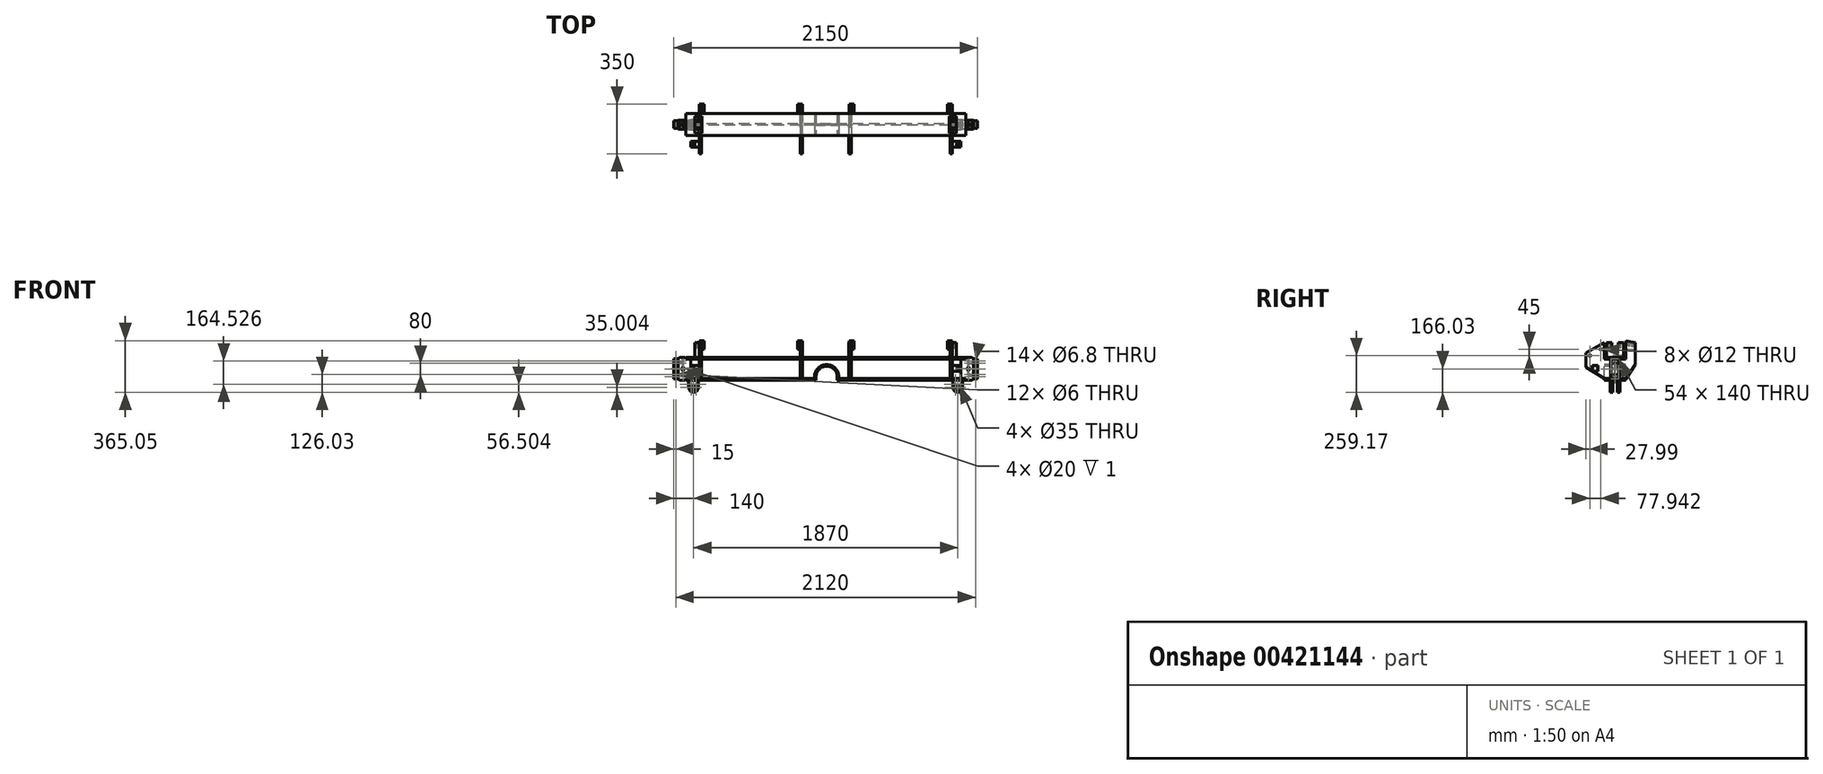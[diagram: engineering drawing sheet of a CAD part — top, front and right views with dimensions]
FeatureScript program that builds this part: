
annotation { "Feature Type Name" : "Feature", "Feature Type Description" : "" }
export const myFeature = defineFeature(function(context is Context, id is Id, definition is map)
    precondition{}
    {
        {
            var Q0;
            Q0=qCreatedBy(makeId("Right.planeOp"),FACE);
            var sketch = newSketch(context, id + "F0", { "sketchPlane" : qUnion([Q0])});
            skLineSegment(sketch, "E0.bottom", {"start": v(-77.22, 81.03) * mm, "end": v(77.22, 81.03) * mm});
            skLineSegment(sketch, "E0.top", {"start": v(-77.22, -81.03) * mm, "end": v(77.22, -81.03) * mm});
            skLineSegment(sketch, "E0.left", {"start": v(-77.22, 81.03) * mm, "end": v(-77.22, 69.47) * mm});
            skLineSegment(sketch, "E0.right", {"start": v(77.22, 81.03) * mm, "end": v(77.22, 69.47) * mm});
            skPoint(sketch, "E0.middle", {"position": v(0, 0) * mm});
            skLineSegment(sketch, "E1", {"start": v(0, 87.3) * mm, "end": v(0, -92.44) * mm, "construction": true});
            skLineSegment(sketch, "E2.0", {"start": v(-77.22, 69.47) * mm, "end": v(-16.76, 69.47) * mm});
            skLineSegment(sketch, "E3.0", {"start": v(-77.22, -69.47) * mm, "end": v(-16.76, -69.47) * mm});
            skLineSegment(sketch, "E4.0", {"start": v(-4.06, 56.77) * mm, "end": v(-4.06, -56.77) * mm});
            skLineSegment(sketch, "E5.0", {"start": v(4.06, 56.77) * mm, "end": v(4.06, -56.77) * mm});
            skLineSegment(sketch, "E6.trimOffspring", {"start": v(16.76, -69.47) * mm, "end": v(77.22, -69.47) * mm});
            skLineSegment(sketch, "E7.trimOffspring", {"start": v(16.76, 69.47) * mm, "end": v(77.22, 69.47) * mm});
            skLineSegment(sketch, "E8.trimOffspring", {"start": v(-77.22, -69.47) * mm, "end": v(-77.22, -81.03) * mm});
            skLineSegment(sketch, "E9.trimOffspring", {"start": v(77.22, -69.47) * mm, "end": v(77.22, -81.03) * mm});
            skPoint(sketch, "E10.visualSharp", {"position": v(-4.06, 69.47) * mm});
            skArc(sketch, "E10.filletArc", {"start": v(-4.06, 56.77) * mm, "mid": v(-7.78, 65.75) * mm, "end": v(-16.76, 69.47) * mm});
            skPoint(sketch, "E11.visualSharp", {"position": v(4.06, 69.47) * mm});
            skArc(sketch, "E11.filletArc", {"start": v(16.76, 69.47) * mm, "mid": v(7.78, 65.75) * mm, "end": v(4.06, 56.77) * mm});
            skPoint(sketch, "E12.visualSharp", {"position": v(4.06, -69.47) * mm});
            skArc(sketch, "E12.filletArc", {"start": v(4.06, -56.77) * mm, "mid": v(7.78, -65.75) * mm, "end": v(16.76, -69.47) * mm});
            skPoint(sketch, "E13.visualSharp", {"position": v(-4.06, -69.47) * mm});
            skArc(sketch, "E13.filletArc", {"start": v(-16.76, -69.47) * mm, "mid": v(-7.78, -65.75) * mm, "end": v(-4.06, -56.77) * mm});
            skSolve(sketch);
        }
        {
            var Q0;
            Q0=qSketchRegion(id+"F0",true);
            extrude(context, id + "F1", {"entities" : qUnion([Q0]), "endBound" : BoundingType.SYMMETRIC, "depth" : 1980 * mm});
        }
        {
            var Q0;
            Q0=makeQuery(id+"F1.opExtrude","SWEPT_FACE",FACE,{"disambiguationData":[OSD([sQuery(id+"F0.wireOp",EDGE,"E4.0")])]});
            var sketch = newSketch(context, id + "F2", { "sketchPlane" : qUnion([Q0])});
            skLineSegment(sketch, "E14", {"start": v(0, 173.84) * mm, "end": v(0, -192.2) * mm, "construction": true});
            skLineSegment(sketch, "E15.0", {"start": v(-990, 69.47) * mm, "end": v(-990, -69.47) * mm, "construction": true});
            skLineSegment(sketch, "E16.0", {"start": v(990, 69.47) * mm, "end": v(-990, 69.47) * mm, "construction": true});
            skLineSegment(sketch, "E17.0", {"start": v(990, -69.47) * mm, "end": v(-990, -69.47) * mm, "construction": true});
            skPoint(sketch, "E18.orphan", {"position": v(-990, 56.77) * mm});
            skPoint(sketch, "E19.orphan", {"position": v(-990, -56.77) * mm});
            skLineSegment(sketch, "E20.bottom", {"start": v(-990, 69.47) * mm, "end": v(-955, 69.47) * mm});
            skLineSegment(sketch, "E20.top", {"start": v(-990, -69.47) * mm, "end": v(-955, -69.47) * mm});
            skLineSegment(sketch, "E20.left", {"start": v(-990, 69.47) * mm, "end": v(-990, -69.47) * mm});
            skLineSegment(sketch, "E20.right", {"start": v(-955, 69.47) * mm, "end": v(-955, -69.47) * mm});
            skLineSegment(sketch, "E21.MirrorCS", {"start": v(990, -69.47) * mm, "end": v(955, -69.47) * mm});
            skLineSegment(sketch, "E22.MirrorCS", {"start": v(990, 69.47) * mm, "end": v(955, 69.47) * mm});
            skLineSegment(sketch, "E23.MirrorCS", {"start": v(990, 69.47) * mm, "end": v(990, -69.47) * mm});
            skLineSegment(sketch, "E24.MirrorCS", {"start": v(955, 69.47) * mm, "end": v(955, -69.47) * mm});
            skPoint(sketch, "E25.MirrorP", {"position": v(990, -56.77) * mm});
            skPoint(sketch, "E26.MirrorP", {"position": v(990, 56.77) * mm});
            skLineSegment(sketch, "E27.MirrorCS", {"start": v(990, 69.47) * mm, "end": v(990, -69.47) * mm, "construction": true});
            skSolve(sketch);
        }
        {
            var Q0;
            Q0=qSketchRegion(id+"F2",true);
            extrude(context, id + "F3", {"entities" : qUnion([Q0]), "operationType" : NewBodyOperationType.REMOVE, "endBound" : BoundingType.SYMMETRIC, "oppositeDirection" : true, "depth" : 50 * mm});
        }
        {
            var Q0;
            Q0=qCreatedBy(makeId("Front.planeOp"),FACE);
            var sketch = newSketch(context, id + "F4", { "sketchPlane" : qUnion([Q0])});
            skLineSegment(sketch, "E28", {"start": v(0, 276.7) * mm, "end": v(0, -349.05) * mm, "construction": true});
            skLineSegment(sketch, "E29.0", {"start": v(-1075, 276.7) * mm, "end": v(-1075, -349.05) * mm, "construction": true});
            skLineSegment(sketch, "E30.0", {"start": v(990, 81.03) * mm, "end": v(-1045, 81.03) * mm, "construction": true});
            skLineSegment(sketch, "E31.0", {"start": v(990, -81.03) * mm, "end": v(-1045, -81.03) * mm, "construction": true});
            skLineSegment(sketch, "E32.0", {"start": v(-955, -69.47) * mm, "end": v(-955, 69.47) * mm, "construction": true});
            skLineSegment(sketch, "E33.0", {"start": v(990, -69.47) * mm, "end": v(-990, -69.47) * mm, "construction": true});
            skLineSegment(sketch, "E34.0", {"start": v(990, 69.47) * mm, "end": v(-990, 69.47) * mm, "construction": true});
            skPoint(sketch, "E35.orphan", {"position": v(-955, 56.77) * mm});
            skPoint(sketch, "E36.orphan", {"position": v(-955, -56.77) * mm});
            skPoint(sketch, "E37.orphan", {"position": v(-990, 81.03) * mm});
            skPoint(sketch, "E38.orphan", {"position": v(-990, -81.03) * mm});
            skLineSegment(sketch, "E39", {"start": v(-990, 81.03) * mm, "end": v(-990, 69.47) * mm, "construction": true});
            skLineSegment(sketch, "E40.0", {"start": v(-1045, 81.03) * mm, "end": v(-1045, 70) * mm, "construction": true});
            skLineSegment(sketch, "E41", {"start": v(0, 0) * mm, "end": v(-1199.42, 0) * mm, "construction": true});
            skLineSegment(sketch, "E42.0", {"start": v(0, 70) * mm, "end": v(-990, 70) * mm, "construction": true});
            skLineSegment(sketch, "E43.trimOffspring", {"start": v(-1045, 70) * mm, "end": v(-1075, 70) * mm, "construction": true});
            skLineSegment(sketch, "E44.MirrorCS", {"start": v(-1045, -70) * mm, "end": v(-1075, -70) * mm, "construction": true});
            skPoint(sketch, "E45.orphan", {"position": v(-1199.42, 70) * mm});
            skPoint(sketch, "E46.orphan", {"position": v(-1199.42, -70) * mm});
            skLineSegment(sketch, "E47.trimOffspring", {"start": v(-1045, -70) * mm, "end": v(-1045, -81.03) * mm, "construction": true});
            skLineSegment(sketch, "E48.trimOffspring", {"start": v(-990, -69.47) * mm, "end": v(-990, -81.03) * mm, "construction": true});
            skLineSegment(sketch, "E49.bottom", {"start": v(-1075, 70) * mm, "end": v(-1045, 70) * mm});
            skLineSegment(sketch, "E49.top", {"start": v(-1075, -70) * mm, "end": v(-1045, -70) * mm});
            skLineSegment(sketch, "E49.left", {"start": v(-1075, 70) * mm, "end": v(-1075, -70) * mm});
            skLineSegment(sketch, "E50.bottom", {"start": v(-1045, 81.03) * mm, "end": v(-990, 81.03) * mm});
            skLineSegment(sketch, "E50.top", {"start": v(-1045, -81.03) * mm, "end": v(-990, -81.03) * mm});
            skLineSegment(sketch, "E50.left", {"start": v(-1045, 81.03) * mm, "end": v(-1045, 70) * mm});
            skLineSegment(sketch, "E50.right", {"start": v(-990, 81.03) * mm, "end": v(-990, 69.47) * mm});
            skLineSegment(sketch, "E51.bottom", {"start": v(-990, 70) * mm, "end": v(-955, 70) * mm});
            skLineSegment(sketch, "E51.top", {"start": v(-990, -69.47) * mm, "end": v(-955, -69.47) * mm});
            skLineSegment(sketch, "E51.left", {"start": v(-990, 70) * mm, "end": v(-990, 69.47) * mm});
            skLineSegment(sketch, "E51.right", {"start": v(-955, 70) * mm, "end": v(-955, -69.47) * mm});
            skLineSegment(sketch, "E52.trimOffspring", {"start": v(-990, -69.47) * mm, "end": v(-990, -81.03) * mm});
            skLineSegment(sketch, "E53.trimOffspring", {"start": v(-1045, -70) * mm, "end": v(-1045, -81.03) * mm});
            skSolve(sketch);
        }
        {
            var Q0;
            Q0=qSketchRegion(id+"F4",true);
            extrude(context, id + "F5", {"entities" : qUnion([Q0]), "endBound" : BoundingType.SYMMETRIC, "depth" : 63.5 * mm});
        }
        {
            var Q0;
            Q0=makeQuery(id+"F5.opExtrude","SWEPT_FACE",FACE,{"disambiguationData":[OSD([sQuery(id+"F4.wireOp",EDGE,"E49.bottom")])]});
            var sketch = newSketch(context, id + "F6", { "sketchPlane" : qUnion([Q0])});
            skLineSegment(sketch, "E54", {"start": v(-948.4, 0) * mm, "end": v(-1101.52, 0) * mm, "construction": true});
            skLineSegment(sketch, "E55.0", {"start": v(-1045, -31.75) * mm, "end": v(-1045, 31.75) * mm, "construction": true});
            skLineSegment(sketch, "E56.0", {"start": v(-948.4, 27) * mm, "end": v(-1101.52, 27) * mm, "construction": true});
            skLineSegment(sketch, "E57.bottom", {"start": v(-1075, 31.75) * mm, "end": v(-1045, 31.75) * mm});
            skLineSegment(sketch, "E57.top", {"start": v(-1075, 27) * mm, "end": v(-1045, 27) * mm});
            skLineSegment(sketch, "E57.left", {"start": v(-1075, 31.75) * mm, "end": v(-1075, 27) * mm});
            skLineSegment(sketch, "E57.right", {"start": v(-1045, 31.75) * mm, "end": v(-1045, 27) * mm});
            skLineSegment(sketch, "E58.MirrorCS", {"start": v(-1045, -31.75) * mm, "end": v(-1045, -27) * mm});
            skLineSegment(sketch, "E59.MirrorCS", {"start": v(-1075, -31.75) * mm, "end": v(-1075, -27) * mm});
            skLineSegment(sketch, "E60.MirrorCS", {"start": v(-1075, -27) * mm, "end": v(-1045, -27) * mm});
            skLineSegment(sketch, "E61.MirrorCS", {"start": v(-1075, -31.75) * mm, "end": v(-1045, -31.75) * mm});
            skSolve(sketch);
        }
        {
            var Q0;
            Q0=qSketchRegion(id+"F6",true);
            extrude(context, id + "F7", {"entities" : qUnion([Q0]), "operationType" : NewBodyOperationType.REMOVE, "endBound" : BoundingType.THROUGH_ALL, "oppositeDirection" : true, "depth" : 25 * mm});
        }
        {
            var Q0;
            Q0=makeQuery(id+"F5.opExtrude","SWEPT_FACE",FACE,{"disambiguationData":[OSD([sQuery(id+"F4.wireOp",EDGE,"E50.bottom")])]});
            var sketch = newSketch(context, id + "F8", { "sketchPlane" : qUnion([Q0])});
            skLineSegment(sketch, "E62.0", {"start": v(-1075, -27) * mm, "end": v(-1075, 27) * mm, "construction": true});
            skLineSegment(sketch, "E63", {"start": v(-919.6, 0) * mm, "end": v(-1088.25, 0) * mm, "construction": true});
            skPoint(sketch, "E63.endSnap0", {"position": v(-1075, 0) * mm});
            skLineSegment(sketch, "E64.0", {"start": v(-1010, -27) * mm, "end": v(-1010, 27) * mm, "construction": true});
            skPoint(sketch, "E65", {"position": v(-1010, 0) * mm});
            skSolve(sketch);
        }
        {
            var Q0;
            Q0=sQuery(id+"F8.wireOp",VERTEX,"E65");
            var Q1;
            Q1=makeQuery(id+"F5.opExtrude","SWEPT_BODY",BODY,{"disambiguationData":[OSD([sQuery(id+"F4.wireOp",EDGE,"E49.bottom"),sQuery(id+"F4.wireOp",EDGE,"E49.top"),sQuery(id+"F4.wireOp",EDGE,"E49.left"),sQuery(id+"F4.wireOp",EDGE,"E50.bottom"),sQuery(id+"F4.wireOp",EDGE,"E50.top"),sQuery(id+"F4.wireOp",EDGE,"E50.left"),sQuery(id+"F4.wireOp",EDGE,"E50.right"),sQuery(id+"F4.wireOp",EDGE,"E51.bottom"),sQuery(id+"F4.wireOp",EDGE,"E51.top"),sQuery(id+"F4.wireOp",EDGE,"E51.right"),sQuery(id+"F4.wireOp",EDGE,"E52.trimOffspring"),sQuery(id+"F4.wireOp",EDGE,"E53.trimOffspring")])]});
            hole(context, id + "F9", {"style" : HoleStyle.SIMPLE, "endStyle" : HoleEndStyle.BLIND, "standardTappedOrClearance" : lookupTablePath({ "standard" : "ISO", "size" : "6", "type" : "Drilled" }), "standardBlindInLast" : lookupTablePath({ "standard" : "ISO", "size" : "6", "type" : "Drilled" }), "holeDiameter" : 6 * mm, "holeDepth" : 125 * mm, "locations" : qUnion([Q0]), "scope" : qUnion([Q1])});
        }
        {
            var Q0;
            Q0=sQuery(id+"F8.wireOp",VERTEX,"E65");
            var Q1;
            Q1=makeQuery(id+"F5.opExtrude","SWEPT_BODY",BODY,{"disambiguationData":[OSD([sQuery(id+"F4.wireOp",EDGE,"E49.bottom"),sQuery(id+"F4.wireOp",EDGE,"E49.top"),sQuery(id+"F4.wireOp",EDGE,"E49.left"),sQuery(id+"F4.wireOp",EDGE,"E50.bottom"),sQuery(id+"F4.wireOp",EDGE,"E50.top"),sQuery(id+"F4.wireOp",EDGE,"E50.left"),sQuery(id+"F4.wireOp",EDGE,"E50.right"),sQuery(id+"F4.wireOp",EDGE,"E51.bottom"),sQuery(id+"F4.wireOp",EDGE,"E51.top"),sQuery(id+"F4.wireOp",EDGE,"E51.right"),sQuery(id+"F4.wireOp",EDGE,"E52.trimOffspring"),sQuery(id+"F4.wireOp",EDGE,"E53.trimOffspring")])]});
            hole(context, id + "F10", {"style" : HoleStyle.SIMPLE, "endStyle" : HoleEndStyle.BLIND, "standardTappedOrClearance" : lookupTablePath({ "standard" : "ANSI", "engagement" : "75%", "pitch" : "13 tpi", "size" : "1/2", "type" : "Tapped" }), "standardBlindInLast" : lookupTablePath({ "standard" : "ANSI", "engagement" : "75%", "pitch" : "13 tpi", "size" : "1/2", "type" : "Tapped" }), "holeDiameter" : 10.72 * mm, "holeDepth" : 15 * mm, "locations" : qUnion([Q0]), "scope" : qUnion([Q1]), "majorDiameter" : 12.7 * mm});
        }
        {
            var Q0;
            {var subQ0=sQuery(id+"F4.wireOp",EDGE,"E50.bottom");Q0=makeQuery(id+"F8.imprint","IMPRINT",FACE,{"disambiguationData":[TD([[makeQuery(id+"F8.imprint","IMPRINT",EDGE,{"derivedFrom":makeQuery(id+"F5.opExtrude","CAP_EDGE",EDGE,{"disambiguationData":[OSD([subQ0])],"isStart":true})}),-1.0]])]});}
            var sketch = newSketch(context, id + "F11", { "sketchPlane" : qUnion([Q0])});
            skPoint(sketch, "E66.0", {"position": v(-1010, 0) * mm});
            skCircle(sketch, "E67", {"center": v(-1010, 0) * mm, "radius": 10 * mm});
            skSolve(sketch);
        }
        {
            var Q0;
            Q0=qSketchRegion(id+"F11",true);
            extrude(context, id + "F12", {"entities" : qUnion([Q0]), "operationType" : NewBodyOperationType.REMOVE, "oppositeDirection" : true, "depth" : 1 * mm});
        }
        {
            var Q0;
            Q0=makeQuery(id+"F5.opExtrude","SWEPT_EDGE",EDGE,{"disambiguationData":[OSD([sQuery(id+"F4.wireOp",EDGE,"E50.bottom"),sQuery(id+"F4.wireOp",EDGE,"E50.left")])]});
            var Q1;
            Q1=makeQuery(id+"F7.boolean.opBoolean","INTERSECT",EDGE,{"derivedFrom":[makeQuery(id+"F7.opExtrude","SWEPT_FACE",FACE,{"disambiguationData":[OSD([sQuery(id+"F6.wireOp",EDGE,"E57.right")])]}),makeQuery(id+"F7.opExtrude","SWEPT_FACE",FACE,{"disambiguationData":[OSD([sQuery(id+"F6.wireOp",EDGE,"E58.MirrorCS")])]})]});
            chamfer(context, id + "F13", {"entities" : qUnion([Q0, Q1]), "width" : 11 * mm, "tangentPropagation" : true});
        }
        {
            var Q0;
            Q0=makeQuery(id+"F5.opExtrude","CAP_FACE",FACE,{"disambiguationData":[OSD([sQuery(id+"F4.wireOp",EDGE,"E49.bottom"),sQuery(id+"F4.wireOp",EDGE,"E49.top"),sQuery(id+"F4.wireOp",EDGE,"E49.left"),sQuery(id+"F4.wireOp",EDGE,"E50.bottom"),sQuery(id+"F4.wireOp",EDGE,"E50.top"),sQuery(id+"F4.wireOp",EDGE,"E50.left"),sQuery(id+"F4.wireOp",EDGE,"E50.right"),sQuery(id+"F4.wireOp",EDGE,"E51.bottom"),sQuery(id+"F4.wireOp",EDGE,"E51.top"),sQuery(id+"F4.wireOp",EDGE,"E51.right"),sQuery(id+"F4.wireOp",EDGE,"E52.trimOffspring"),sQuery(id+"F4.wireOp",EDGE,"E53.trimOffspring")])],"isStart":false});
            var sketch = newSketch(context, id + "F14", { "sketchPlane" : qUnion([Q0])});
            skLineSegment(sketch, "E68", {"start": v(-947.26, 0.27) * mm, "end": v(-1104.17, 0.27) * mm, "construction": true});
            skPoint(sketch, "E68.startSnap0", {"position": v(-955, 0.27) * mm});
            skLineSegment(sketch, "E69.0", {"start": v(-1075, -70) * mm, "end": v(-1075, 70) * mm, "construction": true});
            skLineSegment(sketch, "E70.0", {"start": v(-1010, -70) * mm, "end": v(-1010, 70) * mm, "construction": true});
            skPoint(sketch, "E71", {"position": v(-1010, 0.27) * mm});
            skSolve(sketch);
        }
        {
            var Q0;
            Q0=sQuery(id+"F14.wireOp",VERTEX,"E71");
            var Q1;
            Q1=makeQuery(id+"F5.opExtrude","SWEPT_BODY",BODY,{"disambiguationData":[OSD([sQuery(id+"F4.wireOp",EDGE,"E49.bottom"),sQuery(id+"F4.wireOp",EDGE,"E49.top"),sQuery(id+"F4.wireOp",EDGE,"E49.left"),sQuery(id+"F4.wireOp",EDGE,"E50.bottom"),sQuery(id+"F4.wireOp",EDGE,"E50.top"),sQuery(id+"F4.wireOp",EDGE,"E50.left"),sQuery(id+"F4.wireOp",EDGE,"E50.right"),sQuery(id+"F4.wireOp",EDGE,"E51.bottom"),sQuery(id+"F4.wireOp",EDGE,"E51.top"),sQuery(id+"F4.wireOp",EDGE,"E51.right"),sQuery(id+"F4.wireOp",EDGE,"E52.trimOffspring"),sQuery(id+"F4.wireOp",EDGE,"E53.trimOffspring")])]});
            hole(context, id + "F15", {"style" : HoleStyle.SIMPLE, "endStyle" : HoleEndStyle.BLIND, "standardTappedOrClearance" : lookupTablePath({ "standard" : "ANSI", "engagement" : "75%", "pitch" : "13 tpi", "size" : "1/2", "type" : "Tapped" }), "standardBlindInLast" : lookupTablePath({ "standard" : "ANSI", "engagement" : "75%", "pitch" : "13 tpi", "size" : "1/2", "type" : "Tapped" }), "holeDiameter" : 10.72 * mm, "holeDepth" : 15 * mm, "locations" : qUnion([Q0]), "scope" : qUnion([Q1]), "majorDiameter" : 12.7 * mm});
        }
        {
            var Q0;
            Q0=sQuery(id+"F14.wireOp",VERTEX,"E71");
            var Q1;
            Q1=makeQuery(id+"F5.opExtrude","SWEPT_BODY",BODY,{"disambiguationData":[OSD([sQuery(id+"F4.wireOp",EDGE,"E49.bottom"),sQuery(id+"F4.wireOp",EDGE,"E49.top"),sQuery(id+"F4.wireOp",EDGE,"E49.left"),sQuery(id+"F4.wireOp",EDGE,"E50.bottom"),sQuery(id+"F4.wireOp",EDGE,"E50.top"),sQuery(id+"F4.wireOp",EDGE,"E50.left"),sQuery(id+"F4.wireOp",EDGE,"E50.right"),sQuery(id+"F4.wireOp",EDGE,"E51.bottom"),sQuery(id+"F4.wireOp",EDGE,"E51.top"),sQuery(id+"F4.wireOp",EDGE,"E51.right"),sQuery(id+"F4.wireOp",EDGE,"E52.trimOffspring"),sQuery(id+"F4.wireOp",EDGE,"E53.trimOffspring")])]});
            hole(context, id + "F16", {"style" : HoleStyle.SIMPLE, "endStyle" : HoleEndStyle.THROUGH, "standardTappedOrClearance" : lookupTablePath({ "standard" : "ISO", "size" : "6", "type" : "Drilled" }), "standardBlindInLast" : lookupTablePath({ "standard" : "ISO", "size" : "6", "type" : "Drilled" }), "holeDiameter" : 6 * mm, "locations" : qUnion([Q0]), "scope" : qUnion([Q1]), "isTappedThrough" : true});
        }
        {
            var Q0;
            {var subQ4=sQuery(id+"F4.wireOp",EDGE,"E50.right");Q0=makeQuery(id+"F14.imprint","IMPRINT",FACE,{"disambiguationData":[TD([[makeQuery(id+"F14.imprint","IMPRINT",EDGE,{"derivedFrom":makeQuery(id+"F5.opExtrude","CAP_EDGE",EDGE,{"disambiguationData":[OSD([subQ4])],"isStart":false})}),-1.0]])]});}
            var sketch = newSketch(context, id + "F17", { "sketchPlane" : qUnion([Q0])});
            skCircle(sketch, "E72", {"center": v(-1010, 0.27) * mm, "radius": 10 * mm});
            skSolve(sketch);
        }
        {
            var Q0;
            Q0=qSketchRegion(id+"F17",true);
            extrude(context, id + "F18", {"entities" : qUnion([Q0]), "operationType" : NewBodyOperationType.REMOVE, "oppositeDirection" : true, "depth" : 1 * mm});
        }
        {
            var Q0;
            Q0=makeQuery(id+"F5.opExtrude","CAP_FACE",FACE,{"disambiguationData":[OSD([sQuery(id+"F4.wireOp",EDGE,"E49.bottom"),sQuery(id+"F4.wireOp",EDGE,"E49.top"),sQuery(id+"F4.wireOp",EDGE,"E49.left"),sQuery(id+"F4.wireOp",EDGE,"E50.bottom"),sQuery(id+"F4.wireOp",EDGE,"E50.top"),sQuery(id+"F4.wireOp",EDGE,"E50.left"),sQuery(id+"F4.wireOp",EDGE,"E50.right"),sQuery(id+"F4.wireOp",EDGE,"E51.bottom"),sQuery(id+"F4.wireOp",EDGE,"E51.top"),sQuery(id+"F4.wireOp",EDGE,"E51.right"),sQuery(id+"F4.wireOp",EDGE,"E52.trimOffspring"),sQuery(id+"F4.wireOp",EDGE,"E53.trimOffspring")])],"isStart":true});
            var sketch = newSketch(context, id + "F19", { "sketchPlane" : qUnion([Q0])});
            skCircle(sketch, "E73.0", {"center": v(1010, 0.27) * mm, "radius": 10 * mm, "construction": true});
            skCircle(sketch, "E74", {"center": v(1010, 0.27) * mm, "radius": 10 * mm});
            skSolve(sketch);
        }
        {
            var Q0;
            Q0=qSketchRegion(id+"F19",true);
            extrude(context, id + "F20", {"entities" : qUnion([Q0]), "operationType" : NewBodyOperationType.REMOVE, "oppositeDirection" : true, "depth" : 1 * mm});
        }
        {
            var Q0;
            Q0=sQuery(id+"F19.wireOp",VERTEX,"E73.0.center");
            var Q1;
            Q1=makeQuery(id+"F5.opExtrude","SWEPT_BODY",BODY,{"disambiguationData":[OSD([sQuery(id+"F4.wireOp",EDGE,"E49.bottom"),sQuery(id+"F4.wireOp",EDGE,"E49.top"),sQuery(id+"F4.wireOp",EDGE,"E49.left"),sQuery(id+"F4.wireOp",EDGE,"E50.bottom"),sQuery(id+"F4.wireOp",EDGE,"E50.top"),sQuery(id+"F4.wireOp",EDGE,"E50.left"),sQuery(id+"F4.wireOp",EDGE,"E50.right"),sQuery(id+"F4.wireOp",EDGE,"E51.bottom"),sQuery(id+"F4.wireOp",EDGE,"E51.top"),sQuery(id+"F4.wireOp",EDGE,"E51.right"),sQuery(id+"F4.wireOp",EDGE,"E52.trimOffspring"),sQuery(id+"F4.wireOp",EDGE,"E53.trimOffspring")])]});
            hole(context, id + "F21", {"style" : HoleStyle.SIMPLE, "endStyle" : HoleEndStyle.BLIND, "standardTappedOrClearance" : lookupTablePath({ "standard" : "ANSI", "engagement" : "75%", "pitch" : "13 tpi", "size" : "1/2", "type" : "Tapped" }), "standardBlindInLast" : lookupTablePath({ "standard" : "ANSI", "engagement" : "75%", "pitch" : "13 tpi", "size" : "1/2", "type" : "Tapped" }), "holeDiameter" : 10.72 * mm, "holeDepth" : 15 * mm, "locations" : qUnion([Q0]), "scope" : qUnion([Q1]), "majorDiameter" : 12.7 * mm});
        }
        {
            var Q0;
            Q0=makeQuery(id+"F7.boolean.opBoolean","COPY",FACE,{"derivedFrom":makeQuery(id+"F7.opExtrude","SWEPT_FACE",FACE,{"disambiguationData":[OSD([sQuery(id+"F6.wireOp",EDGE,"E60.MirrorCS")])]})});
            var sketch = newSketch(context, id + "F22", { "sketchPlane" : qUnion([Q0])});
            skLineSegment(sketch, "E75.0", {"start": v(-1075, -70) * mm, "end": v(-1075, 70) * mm, "construction": true});
            skLineSegment(sketch, "E76.0", {"start": v(-1060, -70) * mm, "end": v(-1060, 70) * mm, "construction": true});
            skLineSegment(sketch, "E77", {"start": v(-1060, 0) * mm, "end": v(-1136.9, 0) * mm, "construction": true});
            skLineSegment(sketch, "E78.0", {"start": v(-1060, 55) * mm, "end": v(-1136.9, 55) * mm, "construction": true});
            skLineSegment(sketch, "E79.0", {"start": v(-1060, -55) * mm, "end": v(-1136.9, -55) * mm, "construction": true});
            skPoint(sketch, "E80", {"position": v(-1060, 55) * mm});
            skPoint(sketch, "E81", {"position": v(-1060, 0) * mm});
            skPoint(sketch, "E82", {"position": v(-1060, -55) * mm});
            skSolve(sketch);
        }
        {
            var Q0;
            Q0=sQuery(id+"F22.wireOp",VERTEX,"E80");
            var Q1;
            Q1=sQuery(id+"F22.wireOp",VERTEX,"E81");
            var Q2;
            Q2=sQuery(id+"F22.wireOp",VERTEX,"E82");
            var Q3;
            Q3=makeQuery(id+"F5.opExtrude","SWEPT_BODY",BODY,{"disambiguationData":[OSD([sQuery(id+"F4.wireOp",EDGE,"E49.bottom"),sQuery(id+"F4.wireOp",EDGE,"E49.top"),sQuery(id+"F4.wireOp",EDGE,"E49.left"),sQuery(id+"F4.wireOp",EDGE,"E50.bottom"),sQuery(id+"F4.wireOp",EDGE,"E50.top"),sQuery(id+"F4.wireOp",EDGE,"E50.left"),sQuery(id+"F4.wireOp",EDGE,"E50.right"),sQuery(id+"F4.wireOp",EDGE,"E51.bottom"),sQuery(id+"F4.wireOp",EDGE,"E51.top"),sQuery(id+"F4.wireOp",EDGE,"E51.right"),sQuery(id+"F4.wireOp",EDGE,"E52.trimOffspring"),sQuery(id+"F4.wireOp",EDGE,"E53.trimOffspring")])]});
            hole(context, id + "F23", {"style" : HoleStyle.SIMPLE, "endStyle" : HoleEndStyle.THROUGH, "standardTappedOrClearance" : lookupTablePath({ "standard" : "ISO", "engagement" : "75%", "pitch" : "1.25 mm", "size" : "M8", "type" : "Tapped" }), "standardBlindInLast" : lookupTablePath({ "standard" : "ISO", "engagement" : "75%", "pitch" : "1.25 mm", "size" : "M8", "type" : "Tapped" }), "holeDiameter" : 6.8 * mm, "locations" : qUnion([Q0, Q1, Q2]), "scope" : qUnion([Q3]), "isTappedThrough" : true, "majorDiameter" : 8 * mm, "showTappedDepth" : true});
        }
        {
            var Q0;
            Q0=makeQuery(id+"F7.boolean.opBoolean","COPY",FACE,{"derivedFrom":makeQuery(id+"F7.opExtrude","SWEPT_FACE",FACE,{"disambiguationData":[OSD([sQuery(id+"F6.wireOp",EDGE,"E60.MirrorCS")])]})});
            var sketch = newSketch(context, id + "F24", { "sketchPlane" : qUnion([Q0])});
            skLineSegment(sketch, "E83.0", {"start": v(-1060, 0) * mm, "end": v(-1136.9, 0) * mm, "construction": true});
            skLineSegment(sketch, "E84.0", {"start": v(-1060, -70) * mm, "end": v(-1060, 70) * mm, "construction": true});
            skLineSegment(sketch, "E85.0", {"start": v(-1060, 40) * mm, "end": v(-1136.9, 40) * mm, "construction": true});
            skPoint(sketch, "E86", {"position": v(-1060, 40) * mm});
            skPoint(sketch, "E87.MirrorP", {"position": v(-1060, -40) * mm});
            skSolve(sketch);
        }
        {
            var Q0;
            Q0=sQuery(id+"F24.wireOp",VERTEX,"E86");
            var Q1;
            Q1=sQuery(id+"F24.wireOp",VERTEX,"E87.MirrorP");
            var Q2;
            Q2=makeQuery(id+"F5.opExtrude","SWEPT_BODY",BODY,{"disambiguationData":[OSD([sQuery(id+"F4.wireOp",EDGE,"E49.bottom"),sQuery(id+"F4.wireOp",EDGE,"E49.top"),sQuery(id+"F4.wireOp",EDGE,"E49.left"),sQuery(id+"F4.wireOp",EDGE,"E50.bottom"),sQuery(id+"F4.wireOp",EDGE,"E50.top"),sQuery(id+"F4.wireOp",EDGE,"E50.left"),sQuery(id+"F4.wireOp",EDGE,"E50.right"),sQuery(id+"F4.wireOp",EDGE,"E51.bottom"),sQuery(id+"F4.wireOp",EDGE,"E51.top"),sQuery(id+"F4.wireOp",EDGE,"E51.right"),sQuery(id+"F4.wireOp",EDGE,"E52.trimOffspring"),sQuery(id+"F4.wireOp",EDGE,"E53.trimOffspring")])]});
            hole(context, id + "F25", {"style" : HoleStyle.SIMPLE, "endStyle" : HoleEndStyle.THROUGH, "standardTappedOrClearance" : lookupTablePath({ "standard" : "ISO", "size" : "6", "type" : "Drilled" }), "standardBlindInLast" : lookupTablePath({ "standard" : "ISO", "size" : "6", "type" : "Drilled" }), "holeDiameter" : 6 * mm, "locations" : qUnion([Q0, Q1]), "scope" : qUnion([Q2]), "isTappedThrough" : true});
        }
        {
            var Q0;
            Q0=makeQuery(id+"F5.opExtrude","SWEPT_FACE",FACE,{"disambiguationData":[OSD([sQuery(id+"F4.wireOp",EDGE,"E49.left")])]});
            var sketch = newSketch(context, id + "F26", { "sketchPlane" : qUnion([Q0])});
            skLineSegment(sketch, "E88.0.0", {"start": v(-27, -70) * mm, "end": v(27, -70) * mm, "construction": true});
            skLineSegment(sketch, "E88.0.1", {"start": v(27, -70) * mm, "end": v(27, 70) * mm, "construction": true});
            skLineSegment(sketch, "E88.0.2", {"start": v(27, 70) * mm, "end": v(-27, 70) * mm, "construction": true});
            skLineSegment(sketch, "E88.0.3", {"start": v(-27, 70) * mm, "end": v(-27, -70) * mm, "construction": true});
            skLineSegment(sketch, "E89", {"start": v(-27, 0) * mm, "end": v(56.48, 0) * mm, "construction": true});
            skPoint(sketch, "E89.endSnap0", {"position": v(-27, 0) * mm});
            skLineSegment(sketch, "E90", {"start": v(0, 96.87) * mm, "end": v(0, -94.28) * mm, "construction": true});
            skLineSegment(sketch, "E91.0", {"start": v(-27, -40) * mm, "end": v(56.48, -40) * mm, "construction": true});
            skPoint(sketch, "E92", {"position": v(0, -40) * mm});
            skPoint(sketch, "E93.MirrorP", {"position": v(0, 40) * mm});
            skSolve(sketch);
        }
        {
            var Q0;
            Q0=sQuery(id+"F26.wireOp",VERTEX,"E93.MirrorP");
            var Q1;
            Q1=sQuery(id+"F26.wireOp",VERTEX,"E92");
            var Q2;
            Q2=makeQuery(id+"F5.opExtrude","SWEPT_BODY",BODY,{"disambiguationData":[OSD([sQuery(id+"F4.wireOp",EDGE,"E49.bottom"),sQuery(id+"F4.wireOp",EDGE,"E49.top"),sQuery(id+"F4.wireOp",EDGE,"E49.left"),sQuery(id+"F4.wireOp",EDGE,"E50.bottom"),sQuery(id+"F4.wireOp",EDGE,"E50.top"),sQuery(id+"F4.wireOp",EDGE,"E50.left"),sQuery(id+"F4.wireOp",EDGE,"E50.right"),sQuery(id+"F4.wireOp",EDGE,"E51.bottom"),sQuery(id+"F4.wireOp",EDGE,"E51.top"),sQuery(id+"F4.wireOp",EDGE,"E51.right"),sQuery(id+"F4.wireOp",EDGE,"E52.trimOffspring"),sQuery(id+"F4.wireOp",EDGE,"E53.trimOffspring")])]});
            hole(context, id + "F27", {"style" : HoleStyle.SIMPLE, "endStyle" : HoleEndStyle.BLIND, "standardTappedOrClearance" : lookupTablePath({ "standard" : "ISO", "size" : "6", "type" : "Drilled" }), "standardBlindInLast" : lookupTablePath({ "standard" : "ISO", "size" : "6", "type" : "Drilled" }), "holeDiameter" : 6 * mm, "holeDepth" : 65 * mm, "locations" : qUnion([Q0, Q1]), "scope" : qUnion([Q2])});
        }
        {
            var Q0;
            Q0=sQuery(id+"F26.wireOp",VERTEX,"E93.MirrorP");
            var Q1;
            Q1=sQuery(id+"F26.wireOp",VERTEX,"E92");
            var Q2;
            Q2=makeQuery(id+"F5.opExtrude","SWEPT_BODY",BODY,{"disambiguationData":[OSD([sQuery(id+"F4.wireOp",EDGE,"E49.bottom"),sQuery(id+"F4.wireOp",EDGE,"E49.top"),sQuery(id+"F4.wireOp",EDGE,"E49.left"),sQuery(id+"F4.wireOp",EDGE,"E50.bottom"),sQuery(id+"F4.wireOp",EDGE,"E50.top"),sQuery(id+"F4.wireOp",EDGE,"E50.left"),sQuery(id+"F4.wireOp",EDGE,"E50.right"),sQuery(id+"F4.wireOp",EDGE,"E51.bottom"),sQuery(id+"F4.wireOp",EDGE,"E51.top"),sQuery(id+"F4.wireOp",EDGE,"E51.right"),sQuery(id+"F4.wireOp",EDGE,"E52.trimOffspring"),sQuery(id+"F4.wireOp",EDGE,"E53.trimOffspring")])]});
            hole(context, id + "F28", {"style" : HoleStyle.SIMPLE, "endStyle" : HoleEndStyle.BLIND, "standardTappedOrClearance" : lookupTablePath({ "standard" : "ISO", "engagement" : "75%", "pitch" : "1.25 mm", "size" : "M8", "type" : "Tapped" }), "standardBlindInLast" : lookupTablePath({ "standard" : "ISO", "engagement" : "75%", "pitch" : "1.25 mm", "size" : "M8", "type" : "Tapped" }), "holeDiameter" : 6.8 * mm, "holeDepth" : 12 * mm, "locations" : qUnion([Q0, Q1]), "scope" : qUnion([Q2]), "majorDiameter" : 8 * mm});
        }
        {
            var Q0;
            Q0=makeQuery(id+"F5.opExtrude","SWEPT_BODY",BODY,{"disambiguationData":[OSD([sQuery(id+"F4.wireOp",EDGE,"E49.bottom"),sQuery(id+"F4.wireOp",EDGE,"E49.top"),sQuery(id+"F4.wireOp",EDGE,"E49.left"),sQuery(id+"F4.wireOp",EDGE,"E50.bottom"),sQuery(id+"F4.wireOp",EDGE,"E50.top"),sQuery(id+"F4.wireOp",EDGE,"E50.left"),sQuery(id+"F4.wireOp",EDGE,"E50.right"),sQuery(id+"F4.wireOp",EDGE,"E51.bottom"),sQuery(id+"F4.wireOp",EDGE,"E51.top"),sQuery(id+"F4.wireOp",EDGE,"E51.right"),sQuery(id+"F4.wireOp",EDGE,"E52.trimOffspring"),sQuery(id+"F4.wireOp",EDGE,"E53.trimOffspring")])]});
            var Q1;
            Q1=qCreatedBy(makeId("Right.planeOp"),FACE);
            mirror(context, id + "F29", {"entities" : qUnion([Q0]), "mirrorPlane" : qUnion([Q1])});
        }
        {
            var Q0;
            Q0=qCreatedBy(makeId("Front.planeOp"),FACE);
            var sketch = newSketch(context, id + "F30", { "sketchPlane" : qUnion([Q0])});
            skLineSegment(sketch, "E94", {"start": v(0, 217.37) * mm, "end": v(0, -483.51) * mm, "construction": true});
            skLineSegment(sketch, "E95.0", {"start": v(-935, 217.37) * mm, "end": v(-935, -483.51) * mm, "construction": true});
            skLineSegment(sketch, "E96.0.0", {"start": v(-990, -69.47) * mm, "end": v(-990, -81.03) * mm, "construction": true});
            skLineSegment(sketch, "E96.0.1", {"start": v(-990, -81.03) * mm, "end": v(-900, -81.03) * mm});
            skLineSegment(sketch, "E96.0.2", {"start": v(990, -81.03) * mm, "end": v(990, -69.47) * mm, "construction": true});
            skLineSegment(sketch, "E96.0.3", {"start": v(990, -69.47) * mm, "end": v(-990, -69.47) * mm, "construction": true});
            skLineSegment(sketch, "E97.0", {"start": v(-990, -131.03) * mm, "end": v(990, -131.03) * mm, "construction": true});
            skCircle(sketch, "E98", {"center": v(-935, -131.03) * mm, "radius": 17.5 * mm});
            skArc(sketch, "E99", {"start": v(-970, -131.03) * mm, "mid": v(-935, -166.03) * mm, "end": v(-900, -131.03) * mm});
            skLineSegment(sketch, "E100", {"start": v(-970, -131.03) * mm, "end": v(-970, -81.03) * mm});
            skLineSegment(sketch, "E101", {"start": v(-900, -131.03) * mm, "end": v(-900, -81.03) * mm});
            skLineSegment(sketch, "E102.trimOffspring", {"start": v(0, -81.03) * mm, "end": v(990, -81.03) * mm});
            skLineSegment(sketch, "E103", {"start": v(-935, -166.03) * mm, "end": v(-989.6, -166.03) * mm, "construction": true});
            skLineSegment(sketch, "E104.0", {"start": v(-935, -144.53) * mm, "end": v(-989.6, -144.53) * mm, "construction": true});
            skLineSegment(sketch, "E105.0", {"start": v(-990, -109.53) * mm, "end": v(990, -109.53) * mm, "construction": true});
            skLineSegment(sketch, "E106.0", {"start": v(-953, 217.37) * mm, "end": v(-953, -483.51) * mm, "construction": true});
            skPoint(sketch, "E107", {"position": v(-953, -109.53) * mm});
            skPoint(sketch, "E108.MirrorP", {"position": v(-917, -109.53) * mm});
            skSolve(sketch);
        }
        {
            var Q0;
            Q0=qSketchRegion(id+"F30",true);
            extrude(context, id + "F31", {"entities" : qUnion([Q0]), "endBound" : BoundingType.SYMMETRIC, "depth" : 70 * mm});
        }
        {
            var Q0;
            Q0=makeQuery(id+"F31.opExtrude","CAP_FACE",FACE,{"disambiguationData":[OSD([sQuery(id+"F30.wireOp",EDGE,"E96.0.1"),sQuery(id+"F30.wireOp",EDGE,"E98"),sQuery(id+"F30.wireOp",EDGE,"E99"),sQuery(id+"F30.wireOp",EDGE,"E100"),sQuery(id+"F30.wireOp",EDGE,"E101")])],"isStart":false});
            var sketch = newSketch(context, id + "F32", { "sketchPlane" : qUnion([Q0])});
            skPoint(sketch, "E109.0", {"position": v(-953, -109.53) * mm});
            skPoint(sketch, "E110.0", {"position": v(-917, -109.53) * mm});
            skSolve(sketch);
        }
        {
            var Q0;
            Q0=sQuery(id+"F32.wireOp",VERTEX,"E109.0");
            var Q1;
            Q1=sQuery(id+"F32.wireOp",VERTEX,"E110.0");
            var Q2;
            Q2=makeQuery(id+"F31.opExtrude","SWEPT_BODY",BODY,{"disambiguationData":[OSD([sQuery(id+"F30.wireOp",EDGE,"E96.0.1"),sQuery(id+"F30.wireOp",EDGE,"E98"),sQuery(id+"F30.wireOp",EDGE,"E99"),sQuery(id+"F30.wireOp",EDGE,"E100"),sQuery(id+"F30.wireOp",EDGE,"E101")])]});
            hole(context, id + "F33", {"style" : HoleStyle.SIMPLE, "endStyle" : HoleEndStyle.THROUGH, "standardTappedOrClearance" : lookupTablePath({ "standard" : "ISO", "engagement" : "75%", "pitch" : "1.25 mm", "size" : "M8", "type" : "Tapped" }), "standardBlindInLast" : lookupTablePath({ "standard" : "ISO", "engagement" : "75%", "pitch" : "1.25 mm", "size" : "M8", "type" : "Tapped" }), "holeDiameter" : 6.8 * mm, "locations" : qUnion([Q0, Q1]), "scope" : qUnion([Q2]), "isTappedThrough" : true, "majorDiameter" : 8 * mm, "showTappedDepth" : true});
        }
        {
            var Q0;
            Q0=makeQuery(id+"F31.opExtrude","SWEPT_FACE",FACE,{"disambiguationData":[OSD([sQuery(id+"F30.wireOp",EDGE,"E101")])]});
            var sketch = newSketch(context, id + "F34", { "sketchPlane" : qUnion([Q0])});
            skLineSegment(sketch, "E111.0", {"start": v(-35, -81.03) * mm, "end": v(35, -81.03) * mm, "construction": true});
            skLineSegment(sketch, "E112", {"start": v(0, -81.03) * mm, "end": v(0, -181.86) * mm, "construction": true});
            skPoint(sketch, "E112.endSnap0", {"position": v(0, -81.03) * mm});
            skLineSegment(sketch, "E113.0", {"start": v(-15.5, -81.03) * mm, "end": v(-15.5, -181.86) * mm, "construction": true});
            skLineSegment(sketch, "E114", {"start": v(35, -166.03) * mm, "end": v(-35, -166.03) * mm, "construction": true});
            skLineSegment(sketch, "E115.0", {"start": v(35, -148.53) * mm, "end": v(35, -113.53) * mm, "construction": true});
            skLineSegment(sketch, "E116", {"start": v(35, -131.03) * mm, "end": v(-53.23, -131.03) * mm, "construction": true});
            skLineSegment(sketch, "E117.0", {"start": v(35, -87.03) * mm, "end": v(-53.23, -87.03) * mm, "construction": true});
            skLineSegment(sketch, "E118.bottom", {"start": v(-15.5, -166.03) * mm, "end": v(15.5, -166.03) * mm});
            skLineSegment(sketch, "E118.top", {"start": v(-15.5, -87.03) * mm, "end": v(15.5, -87.03) * mm});
            skLineSegment(sketch, "E118.left", {"start": v(-15.5, -166.03) * mm, "end": v(-15.5, -87.03) * mm});
            skLineSegment(sketch, "E118.right", {"start": v(15.5, -166.03) * mm, "end": v(15.5, -87.03) * mm});
            skSolve(sketch);
        }
        {
            var Q0;
            Q0=qSketchRegion(id+"F34",true);
            extrude(context, id + "F35", {"entities" : qUnion([Q0]), "operationType" : NewBodyOperationType.REMOVE, "endBound" : BoundingType.THROUGH_ALL, "oppositeDirection" : true, "depth" : 25 * mm});
        }
        {
            var Q0;
            Q0=makeQuery(id+"F35.boolean.opBoolean","COPY",EDGE,{"derivedFrom":makeQuery(id+"F35.opExtrude","SWEPT_EDGE",EDGE,{"disambiguationData":[OSD([sQuery(id+"F34.wireOp",EDGE,"E118.top"),sQuery(id+"F34.wireOp",EDGE,"E118.right")])]})});
            var Q1;
            Q1=makeQuery(id+"F35.boolean.opBoolean","COPY",EDGE,{"derivedFrom":makeQuery(id+"F35.opExtrude","SWEPT_EDGE",EDGE,{"disambiguationData":[OSD([sQuery(id+"F34.wireOp",EDGE,"E118.top"),sQuery(id+"F34.wireOp",EDGE,"E118.left")])]})});
            fillet(context, id + "F36", {"entities" : qUnion([Q0, Q1]), "radius" : 2 * mm, "tangentPropagation" : true, "allowEdgeOverflow" : false});
        }
        {
            var Q0;
            Q0=makeQuery(id+"F31.opExtrude","SWEPT_BODY",BODY,{"disambiguationData":[OSD([sQuery(id+"F30.wireOp",EDGE,"E96.0.1"),sQuery(id+"F30.wireOp",EDGE,"E98"),sQuery(id+"F30.wireOp",EDGE,"E99"),sQuery(id+"F30.wireOp",EDGE,"E100"),sQuery(id+"F30.wireOp",EDGE,"E101")])]});
            var Q1;
            Q1=qCreatedBy(makeId("Right.planeOp"),FACE);
            mirror(context, id + "F37", {"entities" : qUnion([Q0]), "mirrorPlane" : qUnion([Q1])});
        }
        {
            var Q0;
            Q0=makeQuery(id+"F1.opExtrude","SWEPT_FACE",FACE,{"disambiguationData":[OSD([sQuery(id+"F0.wireOp",EDGE,"E0.bottom")])]});
            var sketch = newSketch(context, id + "F38", { "sketchPlane" : qUnion([Q0])});
            skLineSegment(sketch, "E119", {"start": v(0, 374.52) * mm, "end": v(0, -390.73) * mm, "construction": true});
            skLineSegment(sketch, "E120.0", {"start": v(-880, 374.52) * mm, "end": v(-880, -390.73) * mm, "construction": true});
            skLineSegment(sketch, "E121.0", {"start": v(-925, 374.52) * mm, "end": v(-925, -390.73) * mm, "construction": true});
            skLineSegment(sketch, "E122.0", {"start": v(-874.2, 374.52) * mm, "end": v(-874.2, -390.73) * mm, "construction": true});
            skPoint(sketch, "E123.endSnap0", {"position": v(0, -8.1) * mm});
            skLineSegment(sketch, "E124.0.0", {"start": v(-990, 77.22) * mm, "end": v(-990, -77.22) * mm, "construction": true});
            skLineSegment(sketch, "E124.0.1", {"start": v(-990, -77.22) * mm, "end": v(990, -77.22) * mm, "construction": true});
            skLineSegment(sketch, "E124.0.2", {"start": v(990, -77.22) * mm, "end": v(990, 77.22) * mm, "construction": true});
            skLineSegment(sketch, "E124.0.3", {"start": v(990, 77.22) * mm, "end": v(-990, 77.22) * mm, "construction": true});
            skLineSegment(sketch, "E125", {"start": v(-990, 0) * mm, "end": v(-602.18, 0) * mm, "construction": true});
            skLineSegment(sketch, "E126.0", {"start": v(-990, 60) * mm, "end": v(-602.18, 60) * mm, "construction": true});
            skLineSegment(sketch, "E127.bottom", {"start": v(-925, 60) * mm, "end": v(-874.2, 60) * mm});
            skLineSegment(sketch, "E127.top", {"start": v(-925, -60) * mm, "end": v(-874.2, -60) * mm});
            skLineSegment(sketch, "E127.left", {"start": v(-925, 60) * mm, "end": v(-925, -60) * mm});
            skLineSegment(sketch, "E127.right", {"start": v(-874.2, 60) * mm, "end": v(-874.2, -60) * mm});
            skSolve(sketch);
        }
        {
            var Q0;
            Q0=qSketchRegion(id+"F38",true);
            extrude(context, id + "F39", {"entities" : qUnion([Q0]), "depth" : 120 * mm});
        }
        {
            var Q0;
            Q0=makeQuery(id+"F39.opExtrude","SWEPT_FACE",FACE,{"disambiguationData":[OSD([sQuery(id+"F38.wireOp",EDGE,"E127.left")])]});
            var sketch = newSketch(context, id + "F40", { "sketchPlane" : qUnion([Q0])});
            skLineSegment(sketch, "E128.0", {"start": v(35, -113.53) * mm, "end": v(35, -148.53) * mm, "construction": true});
            skLineSegment(sketch, "E129", {"start": v(35, -131.03) * mm, "end": v(-153.9, -131.03) * mm, "construction": true});
            skLineSegment(sketch, "E130.0", {"start": v(35, 168.97) * mm, "end": v(-153.9, 168.97) * mm, "construction": true});
            skLineSegment(sketch, "E131.0", {"start": v(-60, 201.03) * mm, "end": v(60, 201.03) * mm});
            skLineSegment(sketch, "E132", {"start": v(0, 201.03) * mm, "end": v(0, 143.76) * mm, "construction": true});
            skPoint(sketch, "E132.endSnap0", {"position": v(0, 201.03) * mm});
            skArc(sketch, "E133", {"start": v(-22.5, 168.97) * mm, "mid": v(0, 146.47) * mm, "end": v(22.5, 168.97) * mm});
            skLineSegment(sketch, "E134.0", {"start": v(60, 185.97) * mm, "end": v(22.5, 185.97) * mm});
            skLineSegment(sketch, "E135", {"start": v(-22.5, 168.97) * mm, "end": v(-22.5, 185.97) * mm});
            skLineSegment(sketch, "E136", {"start": v(22.5, 168.97) * mm, "end": v(22.5, 185.97) * mm});
            skLineSegment(sketch, "E137.0", {"start": v(60, 201.03) * mm, "end": v(60, 185.97) * mm});
            skLineSegment(sketch, "E138.0", {"start": v(-60, 201.03) * mm, "end": v(-60, 185.97) * mm});
            skPoint(sketch, "E139.orphan", {"position": v(-60, 81.03) * mm});
            skPoint(sketch, "E140.orphan", {"position": v(60, 81.03) * mm});
            skLineSegment(sketch, "E141.trimOffspring", {"start": v(-22.5, 185.97) * mm, "end": v(-60, 185.97) * mm});
            skSolve(sketch);
        }
        {
            var Q0;
            Q0=qSketchRegion(id+"F40",true);
            extrude(context, id + "F41", {"entities" : qUnion([Q0]), "operationType" : NewBodyOperationType.REMOVE, "endBound" : BoundingType.THROUGH_ALL, "oppositeDirection" : true, "depth" : 25 * mm});
        }
        {
            var Q0;
            Q0=makeQuery(id+"F41.boolean.opBoolean","COPY",FACE,{"derivedFrom":makeQuery(id+"F41.opExtrude","SWEPT_FACE",FACE,{"disambiguationData":[OSD([sQuery(id+"F40.wireOp",EDGE,"E141.trimOffspring")])]})});
            var sketch = newSketch(context, id + "F42", { "sketchPlane" : qUnion([Q0])});
            skLineSegment(sketch, "E142.0", {"start": v(-874.2, 60) * mm, "end": v(-874.2, 22.5) * mm, "construction": true});
            skLineSegment(sketch, "E143.0", {"start": v(-874.2, -60) * mm, "end": v(-925, -60) * mm, "construction": true});
            skLineSegment(sketch, "E144.bottom", {"start": v(-874.2, 60) * mm, "end": v(-880, 60) * mm});
            skLineSegment(sketch, "E144.top", {"start": v(-874.2, -60) * mm, "end": v(-880, -60) * mm});
            skLineSegment(sketch, "E144.left", {"start": v(-874.2, 60) * mm, "end": v(-874.2, -60) * mm});
            skLineSegment(sketch, "E144.right", {"start": v(-880, 60) * mm, "end": v(-880, -60) * mm});
            skLineSegment(sketch, "E145.0", {"start": v(-925, 22.5) * mm, "end": v(-925, 60) * mm, "construction": true});
            skSolve(sketch);
        }
        {
            var Q0;
            Q0=qSketchRegion(id+"F42",true);
            extrude(context, id + "F43", {"entities" : qUnion([Q0]), "operationType" : NewBodyOperationType.REMOVE, "oppositeDirection" : true, "depth" : 92 * mm});
        }
        {
            var Q0;
            Q0=makeQuery(id+"F41.boolean.opBoolean","COPY",FACE,{"derivedFrom":makeQuery(id+"F41.opExtrude","SWEPT_FACE",FACE,{"disambiguationData":[OSD([sQuery(id+"F40.wireOp",EDGE,"E141.trimOffspring")])]})});
            var sketch = newSketch(context, id + "F44", { "sketchPlane" : qUnion([Q0])});
            skLineSegment(sketch, "E146.0.0", {"start": v(-880, 22.5) * mm, "end": v(-880, 60) * mm, "construction": true});
            skLineSegment(sketch, "E146.0.1", {"start": v(-880, 60) * mm, "end": v(-925, 60) * mm, "construction": true});
            skLineSegment(sketch, "E146.0.2", {"start": v(-925, 60) * mm, "end": v(-925, 22.5) * mm, "construction": true});
            skLineSegment(sketch, "E146.0.3", {"start": v(-925, 22.5) * mm, "end": v(-880, 22.5) * mm, "construction": true});
            skLineSegment(sketch, "E147.0.0", {"start": v(-880, -60) * mm, "end": v(-880, -22.5) * mm, "construction": true});
            skLineSegment(sketch, "E147.0.1", {"start": v(-880, -22.5) * mm, "end": v(-925, -22.5) * mm, "construction": true});
            skLineSegment(sketch, "E147.0.2", {"start": v(-925, -22.5) * mm, "end": v(-925, -60) * mm, "construction": true});
            skLineSegment(sketch, "E147.0.3", {"start": v(-925, -60) * mm, "end": v(-880, -60) * mm, "construction": true});
            skLineSegment(sketch, "E148", {"start": v(-902.5, 60) * mm, "end": v(-902.5, -60) * mm, "construction": true});
            skLineSegment(sketch, "E149", {"start": v(-902.5, 0) * mm, "end": v(-937.6, 0) * mm, "construction": true});
            skLineSegment(sketch, "E150.0", {"start": v(-902.5, 37.5) * mm, "end": v(-937.6, 37.5) * mm, "construction": true});
            skPoint(sketch, "E151", {"position": v(-902.5, 37.5) * mm});
            skPoint(sketch, "E152.MirrorP", {"position": v(-902.5, -37.5) * mm});
            skSolve(sketch);
        }
        {
            var Q0;
            Q0=sQuery(id+"F44.wireOp",VERTEX,"E151");
            var Q1;
            Q1=sQuery(id+"F44.wireOp",VERTEX,"E152.MirrorP");
            var Q2;
            Q2=makeQuery(id+"F39.opExtrude","SWEPT_BODY",BODY,{"disambiguationData":[OSD([sQuery(id+"F38.wireOp",EDGE,"E127.bottom"),sQuery(id+"F38.wireOp",EDGE,"E127.top"),sQuery(id+"F38.wireOp",EDGE,"E127.left"),sQuery(id+"F38.wireOp",EDGE,"E127.right")])]});
            hole(context, id + "F45", {"style" : HoleStyle.SIMPLE, "endStyle" : HoleEndStyle.BLIND, "standardTappedOrClearance" : lookupTablePath({ "standard" : "ISO", "engagement" : "75%", "pitch" : "1.25 mm", "size" : "M12", "type" : "Tapped" }), "standardBlindInLast" : lookupTablePath({ "standard" : "ISO", "engagement" : "75%", "pitch" : "1.25 mm", "size" : "M12", "type" : "Tapped" }), "holeDiameter" : 10.8 * mm, "holeDepth" : 35 * mm, "locations" : qUnion([Q0, Q1]), "scope" : qUnion([Q2]), "majorDiameter" : 12 * mm});
        }
        {
            var Q0;
            Q0=makeQuery(id+"F39.opExtrude","SWEPT_BODY",BODY,{"disambiguationData":[OSD([sQuery(id+"F38.wireOp",EDGE,"E127.bottom"),sQuery(id+"F38.wireOp",EDGE,"E127.top"),sQuery(id+"F38.wireOp",EDGE,"E127.left"),sQuery(id+"F38.wireOp",EDGE,"E127.right")])]});
            var Q1;
            Q1=qCreatedBy(makeId("Right.planeOp"),FACE);
            mirror(context, id + "F46", {"entities" : qUnion([Q0]), "mirrorPlane" : qUnion([Q1])});
        }
        {
            var Q0;
            Q0=qCreatedBy(makeId("Right.planeOp"),FACE);
            cPlane(context, id + "F47", {"entities" : qUnion([Q0]), "cplaneType" : CPlaneType.OFFSET, "offset" : (330 / 2 + 15) * mm, "width" : 150 * mm, "height" : 150 * mm});
        }
        {
            var Q0;
            Q0=qCreatedBy(id+"F47.planeOp",FACE);
            var sketch = newSketch(context, id + "F48", { "sketchPlane" : qUnion([Q0])});
            skLineSegment(sketch, "E153", {"start": v(0, 256.72) * mm, "end": v(0, -431.7) * mm, "construction": true});
            skLineSegment(sketch, "E154.0.0", {"start": v(-60, 81.03) * mm, "end": v(-60, 185.97) * mm, "construction": true});
            skLineSegment(sketch, "E154.0.1", {"start": v(-60, 185.97) * mm, "end": v(-22.5, 185.97) * mm, "construction": true});
            skLineSegment(sketch, "E154.0.2", {"start": v(-22.5, 185.97) * mm, "end": v(-22.5, 168.97) * mm, "construction": true});
            skArc(sketch, "E154.0.3", {"start": v(-22.5, 168.97) * mm, "mid": v(0, 146.47) * mm, "end": v(22.5, 168.97) * mm, "construction": true});
            skLineSegment(sketch, "E154.0.4", {"start": v(22.5, 168.97) * mm, "end": v(22.5, 185.97) * mm, "construction": true});
            skLineSegment(sketch, "E154.0.5", {"start": v(22.5, 185.97) * mm, "end": v(144, 185.97) * mm, "construction": true});
            skLineSegment(sketch, "E154.0.6", {"start": v(60, 185.97) * mm, "end": v(60, 81.03) * mm, "construction": true});
            skLineSegment(sketch, "E154.0.7", {"start": v(60, 81.03) * mm, "end": v(-60, 81.03) * mm, "construction": true});
            skLineSegment(sketch, "E155.0", {"start": v(144, 256.72) * mm, "end": v(144, -69.47) * mm});
            skLineSegment(sketch, "E156.0.0", {"start": v(77.22, 81.03) * mm, "end": v(77.22, 69.47) * mm, "construction": true});
            skLineSegment(sketch, "E156.0.1", {"start": v(77.22, 69.47) * mm, "end": v(-77.22, 69.47) * mm, "construction": true});
            skLineSegment(sketch, "E156.0.2", {"start": v(-77.22, 69.47) * mm, "end": v(-77.22, 81.03) * mm, "construction": true});
            skLineSegment(sketch, "E156.0.3", {"start": v(-77.22, 81.03) * mm, "end": v(77.22, 81.03) * mm, "construction": true});
            skLineSegment(sketch, "E157.0.0", {"start": v(-77.22, -69.47) * mm, "end": v(144, -69.47) * mm, "construction": true});
            skLineSegment(sketch, "E157.0.1", {"start": v(77.22, -69.47) * mm, "end": v(77.22, -81.03) * mm, "construction": true});
            skLineSegment(sketch, "E157.0.2", {"start": v(77.22, -81.03) * mm, "end": v(-77.22, -81.03) * mm, "construction": true});
            skLineSegment(sketch, "E157.0.3", {"start": v(-77.22, -81.03) * mm, "end": v(-77.22, -69.47) * mm, "construction": true});
            skLineSegment(sketch, "E158.0.0", {"start": v(16.76, -69.47) * mm, "end": v(-16.76, -69.47) * mm, "construction": true});
            skArc(sketch, "E158.0.1", {"start": v(-16.76, -69.47) * mm, "mid": v(-7.78, -65.75) * mm, "end": v(-4.06, -56.77) * mm, "construction": true});
            skLineSegment(sketch, "E158.0.2", {"start": v(-4.06, -56.77) * mm, "end": v(-4.06, 56.77) * mm, "construction": true});
            skArc(sketch, "E158.0.3", {"start": v(-4.06, 56.77) * mm, "mid": v(-7.78, 65.75) * mm, "end": v(-16.76, 69.47) * mm, "construction": true});
            skLineSegment(sketch, "E158.0.4", {"start": v(-16.76, 69.47) * mm, "end": v(16.76, 69.47) * mm, "construction": true});
            skArc(sketch, "E158.0.5", {"start": v(16.76, 69.47) * mm, "mid": v(7.78, 65.75) * mm, "end": v(4.06, 56.77) * mm, "construction": true});
            skLineSegment(sketch, "E158.0.6", {"start": v(4.06, 56.77) * mm, "end": v(4.06, -56.77) * mm, "construction": true});
            skArc(sketch, "E158.0.7", {"start": v(4.06, -56.77) * mm, "mid": v(7.78, -65.75) * mm, "end": v(16.76, -69.47) * mm, "construction": true});
            skLineSegment(sketch, "E159", {"start": v(144, 185.97) * mm, "end": v(77.22, 197.75) * mm});
            skLineSegment(sketch, "E160.0", {"start": v(70, 86.03) * mm, "end": v(77.22, 86.03) * mm, "construction": true});
            skLineSegment(sketch, "E161.0", {"start": v(77.22, 199.02) * mm, "end": v(77.22, 69.47) * mm});
            skLineSegment(sketch, "E162", {"start": v(144, 30.53) * mm, "end": v(80.74, -69.47) * mm});
            skLineSegment(sketch, "E163", {"start": v(80.74, -69.47) * mm, "end": v(16.76, -69.47) * mm});
            skLineSegment(sketch, "E164", {"start": v(16.76, -69.47) * mm, "end": v(4.06, -56.77) * mm});
            skLineSegment(sketch, "E165", {"start": v(4.06, -56.77) * mm, "end": v(4.06, 56.77) * mm});
            skLineSegment(sketch, "E166", {"start": v(4.06, 56.77) * mm, "end": v(16.76, 69.47) * mm});
            skLineSegment(sketch, "E167", {"start": v(16.76, 69.47) * mm, "end": v(77.22, 69.47) * mm});
            skLineSegment(sketch, "E168", {"start": v(77.22, 69.47) * mm, "end": v(77.22, 86.03) * mm});
            skLineSegment(sketch, "E169", {"start": v(77.22, 86.03) * mm, "end": v(70, 86.03) * mm});
            skLineSegment(sketch, "E170", {"start": v(70, 185.97) * mm, "end": v(70, 199.02) * mm});
            skLineSegment(sketch, "E171", {"start": v(144, 185.97) * mm, "end": v(144, 30.53) * mm});
            skLineSegment(sketch, "E172", {"start": v(77.22, 199.02) * mm, "end": v(91.33, 199.02) * mm});
            skLineSegment(sketch, "E173", {"start": v(77.22, 199.02) * mm, "end": v(150.28, 186.14) * mm});
            skSolve(sketch);
        }
        {
            var Q0;
            Q0=qSketchRegion(id+"F48",true);
            extrude(context, id + "F49", {"entities" : qUnion([Q0]), "oppositeDirection" : true, "depth" : 15.88 * mm});
        }
        {
            var Q0;
            Q0=makeQuery(id+"F49.opExtrude","CAP_FACE",FACE,{"disambiguationData":[OSD([sQuery(id+"F48.wireOp",EDGE,"E159"),sQuery(id+"F48.wireOp",EDGE,"E162"),sQuery(id+"F48.wireOp",EDGE,"E163"),sQuery(id+"F48.wireOp",EDGE,"E164"),sQuery(id+"F48.wireOp",EDGE,"E165"),sQuery(id+"F48.wireOp",EDGE,"E166"),sQuery(id+"F48.wireOp",EDGE,"E167"),sQuery(id+"F48.wireOp",EDGE,"E168"),sQuery(id+"F48.wireOp",EDGE,"E169"),sQuery(id+"F48.wireOp",EDGE,"E170"),sQuery(id+"F48.wireOp",EDGE,"E171")])],"isStart":true});
            var sketch = newSketch(context, id + "F50", { "sketchPlane" : qUnion([Q0])});
            skLineSegment(sketch, "E174.0.4", {"start": v(80.74, -69.47) * mm, "end": v(144, 30.53) * mm});
            skLineSegment(sketch, "E174.0.5", {"start": v(16.76, -69.47) * mm, "end": v(80.74, -69.47) * mm});
            skLineSegment(sketch, "E174.0.6", {"start": v(4.06, -56.77) * mm, "end": v(16.76, -69.47) * mm});
            skLineSegment(sketch, "E174.0.7", {"start": v(4.06, 56.77) * mm, "end": v(4.06, -56.77) * mm});
            skLineSegment(sketch, "E174.0.8", {"start": v(16.76, 69.47) * mm, "end": v(4.06, 56.77) * mm});
            skLineSegment(sketch, "E174.0.9", {"start": v(77.22, 69.47) * mm, "end": v(16.76, 69.47) * mm});
            skLineSegment(sketch, "E174.0.10", {"start": v(77.22, 86.03) * mm, "end": v(77.22, 69.47) * mm});
            skLineSegment(sketch, "E175.0.0", {"start": v(144, 187.25) * mm, "end": v(77.22, 199.02) * mm});
            skLineSegment(sketch, "E175.0.1", {"start": v(77.22, 199.02) * mm, "end": v(77.22, 137.25) * mm});
            skLineSegment(sketch, "E175.0.8", {"start": v(144, 137.25) * mm, "end": v(144, 187.25) * mm});
            skLineSegment(sketch, "E176", {"start": v(77.22, 137.25) * mm, "end": v(144, 137.25) * mm});
            skSolve(sketch);
        }
        {
            var Q0;
            Q0=qSketchRegion(id+"F50",true);
            extrude(context, id + "F51", {"entities" : qUnion([Q0]), "depth" : 19 * mm});
        }
        {
            var Q0;
            Q0=makeQuery(id+"F51.opExtrude","SWEPT_FACE",FACE,{"disambiguationData":[OSD([sQuery(id+"F50.wireOp",EDGE,"E175.0.0")])]});
            var sketch = newSketch(context, id + "F52", { "sketchPlane" : qUnion([Q0])});
            skLineSegment(sketch, "E177", {"start": v(0, 185.79) * mm, "end": v(0, -149.3) * mm, "construction": true});
            skLineSegment(sketch, "E178.0", {"start": v(190, 185.79) * mm, "end": v(190, -149.3) * mm, "construction": true});
            skLineSegment(sketch, "E179.0.0", {"start": v(180, 109.52) * mm, "end": v(180, 34.38) * mm, "construction": true});
            skLineSegment(sketch, "E179.0.1", {"start": v(180, 34.38) * mm, "end": v(205.4, 34.38) * mm, "construction": true});
            skLineSegment(sketch, "E179.0.2", {"start": v(205.4, 34.38) * mm, "end": v(205.4, 109.52) * mm, "construction": true});
            skLineSegment(sketch, "E179.0.3", {"start": v(205.4, 109.52) * mm, "end": v(180, 109.52) * mm, "construction": true});
            skLineSegment(sketch, "E180.0", {"start": v(205.4, 69.52) * mm, "end": v(180, 69.52) * mm, "construction": true});
            skLineSegment(sketch, "E181.0", {"start": v(205.4, 94.52) * mm, "end": v(180, 94.52) * mm, "construction": true});
            skPoint(sketch, "E182", {"position": v(190, 94.52) * mm});
            skPoint(sketch, "E183", {"position": v(190, 69.52) * mm});
            skSolve(sketch);
        }
        {
            var Q0;
            Q0=sQuery(id+"F52.wireOp",VERTEX,"E182");
            var Q1;
            Q1=sQuery(id+"F52.wireOp",VERTEX,"E183");
            var Q2;
            Q2=makeQuery(id+"F51.opExtrude","SWEPT_BODY",BODY,{"disambiguationData":[OSD([sQuery(id+"F50.wireOp",EDGE,"E175.0.0"),sQuery(id+"F50.wireOp",EDGE,"E175.0.1"),sQuery(id+"F50.wireOp",EDGE,"E175.0.8"),sQuery(id+"F50.wireOp",EDGE,"E176")])]});
            hole(context, id + "F53", {"style" : HoleStyle.SIMPLE, "endStyle" : HoleEndStyle.BLIND, "standardTappedOrClearance" : lookupTablePath({ "standard" : "ISO", "engagement" : "75%", "pitch" : "1.5 mm", "size" : "M12", "type" : "Tapped" }), "standardBlindInLast" : lookupTablePath({ "standard" : "ISO", "engagement" : "75%", "pitch" : "1.5 mm", "size" : "M12", "type" : "Tapped" }), "holeDiameter" : 10.5 * mm, "holeDepth" : 30 * mm, "locations" : qUnion([Q0, Q1]), "scope" : qUnion([Q2]), "majorDiameter" : 12 * mm});
        }
        {
            var Q0;
            Q0=makeQuery(id+"F49.opExtrude","SWEPT_BODY",BODY,{"disambiguationData":[OSD([sQuery(id+"F48.wireOp",EDGE,"E159"),sQuery(id+"F48.wireOp",EDGE,"E162"),sQuery(id+"F48.wireOp",EDGE,"E163"),sQuery(id+"F48.wireOp",EDGE,"E164"),sQuery(id+"F48.wireOp",EDGE,"E165"),sQuery(id+"F48.wireOp",EDGE,"E166"),sQuery(id+"F48.wireOp",EDGE,"E167"),sQuery(id+"F48.wireOp",EDGE,"E168"),sQuery(id+"F48.wireOp",EDGE,"E169"),sQuery(id+"F48.wireOp",EDGE,"E170"),sQuery(id+"F48.wireOp",EDGE,"E171")])]});
            var Q1;
            Q1=makeQuery(id+"Fl3NnRKCw4Xixsh_5.opExtrude","SWEPT_BODY",BODY,{"disambiguationData":[OSD([sQuery(id+"F50.wireOp",EDGE,"E174.0.2"),sQuery(id+"F50.wireOp",EDGE,"L5QzTxGx-Pnf6-FATO-cNnD-iBCD0eLFIrfw"),sQuery(id+"F50.wireOp",EDGE,"wuJ0hKJl-j7K5-ufxr-qZVR-Fc0DleJu5Dkg"),sQuery(id+"F50.wireOp",EDGE,"Ftl8TeeW-pfTl-imrB-EIy6-TxBNQzbVambr")])]});
            var Q2;
            Q2=qCreatedBy(makeId("Right.planeOp"),FACE);
            mirror(context, id + "F54", {"entities" : qUnion([Q0, Q1]), "mirrorPlane" : qUnion([Q2])});
        }
        {
            var Q0;
            Q0=qCreatedBy(id+"F47.planeOp",FACE);
            cPlane(context, id + "F55", {"entities" : qUnion([Q0]), "cplaneType" : CPlaneType.OFFSET, "offset" : 350 * mm, "width" : 150 * mm, "height" : 150 * mm});
        }
        {
            var Q0;
            Q0=makeQuery(id+"F49.opExtrude","SWEPT_BODY",BODY,{"disambiguationData":[OSD([sQuery(id+"F48.wireOp",EDGE,"E159"),sQuery(id+"F48.wireOp",EDGE,"E162"),sQuery(id+"F48.wireOp",EDGE,"E163"),sQuery(id+"F48.wireOp",EDGE,"E164"),sQuery(id+"F48.wireOp",EDGE,"E165"),sQuery(id+"F48.wireOp",EDGE,"E166"),sQuery(id+"F48.wireOp",EDGE,"E167"),sQuery(id+"F48.wireOp",EDGE,"E168"),sQuery(id+"F48.wireOp",EDGE,"E169"),sQuery(id+"F48.wireOp",EDGE,"E170"),sQuery(id+"F48.wireOp",EDGE,"E171")])]});
            var Q1;
            Q1=makeQuery(id+"Fl3NnRKCw4Xixsh_5.opExtrude","SWEPT_BODY",BODY,{"disambiguationData":[OSD([sQuery(id+"F50.wireOp",EDGE,"E174.0.2"),sQuery(id+"F50.wireOp",EDGE,"L5QzTxGx-Pnf6-FATO-cNnD-iBCD0eLFIrfw"),sQuery(id+"F50.wireOp",EDGE,"wuJ0hKJl-j7K5-ufxr-qZVR-Fc0DleJu5Dkg"),sQuery(id+"F50.wireOp",EDGE,"Ftl8TeeW-pfTl-imrB-EIy6-TxBNQzbVambr")])]});
            var Q2;
            Q2=qCreatedBy(id+"F55.planeOp",FACE);
            mirror(context, id + "F56", {"entities" : qUnion([Q0, Q1]), "mirrorPlane" : qUnion([Q2])});
        }
        {
            var Q0;
            Q0=makeQuery(id+"F56.opPattern","COPY",BODY,{"derivedFrom":makeQuery(id+"F49.opExtrude","SWEPT_BODY",BODY,{"disambiguationData":[OSD([sQuery(id+"F48.wireOp",EDGE,"E159"),sQuery(id+"F48.wireOp",EDGE,"E162"),sQuery(id+"F48.wireOp",EDGE,"E163"),sQuery(id+"F48.wireOp",EDGE,"E164"),sQuery(id+"F48.wireOp",EDGE,"E165"),sQuery(id+"F48.wireOp",EDGE,"E166"),sQuery(id+"F48.wireOp",EDGE,"E167"),sQuery(id+"F48.wireOp",EDGE,"E168"),sQuery(id+"F48.wireOp",EDGE,"E169"),sQuery(id+"F48.wireOp",EDGE,"E170"),sQuery(id+"F48.wireOp",EDGE,"E171")])]}),"instanceName":"1"});
            var Q1;
            Q1=makeQuery(id+"F56.opPattern","COPY",BODY,{"derivedFrom":makeQuery(id+"Fl3NnRKCw4Xixsh_5.opExtrude","SWEPT_BODY",BODY,{"disambiguationData":[OSD([sQuery(id+"F50.wireOp",EDGE,"E174.0.2"),sQuery(id+"F50.wireOp",EDGE,"L5QzTxGx-Pnf6-FATO-cNnD-iBCD0eLFIrfw"),sQuery(id+"F50.wireOp",EDGE,"wuJ0hKJl-j7K5-ufxr-qZVR-Fc0DleJu5Dkg"),sQuery(id+"F50.wireOp",EDGE,"Ftl8TeeW-pfTl-imrB-EIy6-TxBNQzbVambr")])]}),"instanceName":"1"});
            var Q2;
            Q2=qCreatedBy(makeId("Right.planeOp"),FACE);
            mirror(context, id + "F57", {"entities" : qUnion([Q0, Q1]), "mirrorPlane" : qUnion([Q2])});
        }
        {
            var Q0;
            Q0=qCreatedBy(id+"F47.planeOp",FACE);
            var sketch = newSketch(context, id + "F58", { "sketchPlane" : qUnion([Q0])});
            skLineSegment(sketch, "E184", {"start": v(0, 263.92) * mm, "end": v(0, -250.39) * mm, "construction": true});
            skLineSegment(sketch, "E185.0", {"start": v(-206, 263.92) * mm, "end": v(-206, -250.39) * mm, "construction": true});
            skLineSegment(sketch, "E186.0.0", {"start": v(77.22, 81.03) * mm, "end": v(77.22, 69.47) * mm, "construction": true});
            skLineSegment(sketch, "E186.0.1", {"start": v(77.22, 69.47) * mm, "end": v(-77.22, 69.47) * mm, "construction": true});
            skLineSegment(sketch, "E186.0.2", {"start": v(-77.22, 69.47) * mm, "end": v(-77.22, 81.03) * mm, "construction": true});
            skLineSegment(sketch, "E186.0.3", {"start": v(-77.22, 81.03) * mm, "end": v(77.22, 81.03) * mm, "construction": true});
            skLineSegment(sketch, "E187.0.0", {"start": v(16.76, -69.47) * mm, "end": v(-16.76, -69.47) * mm, "construction": true});
            skArc(sketch, "E187.0.1", {"start": v(-16.76, -69.47) * mm, "mid": v(-7.78, -65.75) * mm, "end": v(-4.06, -56.77) * mm, "construction": true});
            skLineSegment(sketch, "E187.0.2", {"start": v(-4.06, -56.77) * mm, "end": v(-4.06, 56.77) * mm, "construction": true});
            skArc(sketch, "E187.0.3", {"start": v(-4.06, 56.77) * mm, "mid": v(-7.78, 65.75) * mm, "end": v(-16.76, 69.47) * mm, "construction": true});
            skLineSegment(sketch, "E187.0.4", {"start": v(-16.76, 69.47) * mm, "end": v(16.76, 69.47) * mm, "construction": true});
            skArc(sketch, "E187.0.5", {"start": v(16.76, 69.47) * mm, "mid": v(7.78, 65.75) * mm, "end": v(4.06, 56.77) * mm, "construction": true});
            skLineSegment(sketch, "E187.0.6", {"start": v(4.06, 56.77) * mm, "end": v(4.06, -56.77) * mm, "construction": true});
            skArc(sketch, "E187.0.7", {"start": v(4.06, -56.77) * mm, "mid": v(7.78, -65.75) * mm, "end": v(16.76, -69.47) * mm, "construction": true});
            skLineSegment(sketch, "E188.0.0", {"start": v(-77.22, -69.47) * mm, "end": v(77.22, -69.47) * mm, "construction": true});
            skLineSegment(sketch, "E188.0.1", {"start": v(77.22, -69.47) * mm, "end": v(77.22, -81.03) * mm, "construction": true});
            skLineSegment(sketch, "E188.0.2", {"start": v(77.22, -81.03) * mm, "end": v(-77.22, -81.03) * mm, "construction": true});
            skLineSegment(sketch, "E188.0.3", {"start": v(-77.22, -81.03) * mm, "end": v(-77.22, -69.47) * mm, "construction": true});
            skLineSegment(sketch, "E189.0", {"start": v(-206, 10.53) * mm, "end": v(77.22, 10.53) * mm, "construction": true});
            skLineSegment(sketch, "E190", {"start": v(-77.22, 69.47) * mm, "end": v(-16.76, 69.47) * mm});
            skLineSegment(sketch, "E191", {"start": v(-16.76, 69.47) * mm, "end": v(-4.06, 56.77) * mm});
            skLineSegment(sketch, "E192", {"start": v(-4.06, 56.77) * mm, "end": v(-4.06, -56.77) * mm});
            skLineSegment(sketch, "E193", {"start": v(-16.76, -69.47) * mm, "end": v(-4.06, -56.77) * mm});
            skLineSegment(sketch, "E194", {"start": v(-16.76, -69.47) * mm, "end": v(-77.22, -69.47) * mm});
            skLineSegment(sketch, "E195", {"start": v(-77.22, -69.47) * mm, "end": v(-206, 10.53) * mm});
            skLineSegment(sketch, "E196", {"start": v(-77.22, 69.47) * mm, "end": v(-77.22, 185.97) * mm});
            skLineSegment(sketch, "E197.0.0", {"start": v(-60, 81.03) * mm, "end": v(-60, 185.97) * mm});
            skLineSegment(sketch, "E197.0.1", {"start": v(-60, 185.97) * mm, "end": v(-22.5, 185.97) * mm});
            skLineSegment(sketch, "E197.0.2", {"start": v(-22.5, 185.97) * mm, "end": v(-22.5, 168.97) * mm});
            skArc(sketch, "E197.0.3", {"start": v(-22.5, 168.97) * mm, "mid": v(0, 146.47) * mm, "end": v(22.5, 168.97) * mm});
            skLineSegment(sketch, "E197.0.4", {"start": v(22.5, 168.97) * mm, "end": v(22.5, 185.97) * mm});
            skLineSegment(sketch, "E197.0.7", {"start": v(60, 81.03) * mm, "end": v(-60, 81.03) * mm});
            skPoint(sketch, "E197.0.6.start.orphan", {"position": v(60, 185.97) * mm});
            skLineSegment(sketch, "E198", {"start": v(-77.22, 185.97) * mm, "end": v(-222.54, 185.97) * mm, "construction": true});
            skLineSegment(sketch, "E199", {"start": v(-77.22, 185.97) * mm, "end": v(-206, 111.62) * mm});
            skLineSegment(sketch, "E200", {"start": v(-206, 111.62) * mm, "end": v(-206, 10.53) * mm});
            skSolve(sketch);
        }
        {
            var Q0;
            Q0=qSketchRegion(id+"F58",true);
            extrude(context, id + "F59", {"entities" : qUnion([Q0]), "oppositeDirection" : true, "depth" : 16 * mm});
        }
        {
            var Q0;
            Q0=makeQuery(id+"F59.opExtrude","CAP_FACE",FACE,{"disambiguationData":[OSD([sQuery(id+"F58.wireOp",EDGE,"E190"),sQuery(id+"F58.wireOp",EDGE,"E191"),sQuery(id+"F58.wireOp",EDGE,"E192"),sQuery(id+"F58.wireOp",EDGE,"E193"),sQuery(id+"F58.wireOp",EDGE,"E194"),sQuery(id+"F58.wireOp",EDGE,"E195"),sQuery(id+"F58.wireOp",EDGE,"E196"),sQuery(id+"F58.wireOp",EDGE,"E199"),sQuery(id+"F58.wireOp",EDGE,"E200")])],"isStart":false});
            var sketch = newSketch(context, id + "F60", { "sketchPlane" : qUnion([Q0])});
            skLineSegment(sketch, "E201.0.0", {"start": v(206, 111.62) * mm, "end": v(77.22, 185.97) * mm, "construction": true});
            skLineSegment(sketch, "E201.0.1", {"start": v(77.22, 185.97) * mm, "end": v(77.22, 69.47) * mm, "construction": true});
            skLineSegment(sketch, "E201.0.2", {"start": v(77.22, 69.47) * mm, "end": v(16.76, 69.47) * mm, "construction": true});
            skLineSegment(sketch, "E201.0.3", {"start": v(16.76, 69.47) * mm, "end": v(4.06, 56.77) * mm, "construction": true});
            skLineSegment(sketch, "E201.0.4", {"start": v(4.06, 56.77) * mm, "end": v(4.06, -56.77) * mm, "construction": true});
            skLineSegment(sketch, "E201.0.5", {"start": v(4.06, -56.77) * mm, "end": v(16.76, -69.47) * mm, "construction": true});
            skLineSegment(sketch, "E201.0.6", {"start": v(16.76, -69.47) * mm, "end": v(77.22, -69.47) * mm, "construction": true});
            skLineSegment(sketch, "E201.0.7", {"start": v(77.22, -69.47) * mm, "end": v(206, 10.53) * mm, "construction": true});
            skLineSegment(sketch, "E201.0.8", {"start": v(206, 10.53) * mm, "end": v(206, 111.62) * mm, "construction": true});
            skLineSegment(sketch, "E202.0", {"start": v(191, 85.64) * mm, "end": v(62.22, 160) * mm, "construction": true});
            skLineSegment(sketch, "E203", {"start": v(191, 85.64) * mm, "end": v(206, 111.62) * mm, "construction": true});
            skLineSegment(sketch, "E204.0", {"start": v(178, 93.14) * mm, "end": v(193, 119.12) * mm, "construction": true});
            skLineSegment(sketch, "E205.0", {"start": v(100.07, 138.14) * mm, "end": v(115.07, 164.12) * mm, "construction": true});
            skPoint(sketch, "E206", {"position": v(100.07, 138.14) * mm});
            skPoint(sketch, "E207", {"position": v(178, 93.14) * mm});
            skSolve(sketch);
        }
        {
            var Q0;
            Q0=sQuery(id+"F60.wireOp",VERTEX,"E206");
            var Q1;
            Q1=sQuery(id+"F60.wireOp",VERTEX,"E207");
            var Q2;
            Q2=makeQuery(id+"F59.opExtrude","SWEPT_BODY",BODY,{"disambiguationData":[OSD([sQuery(id+"F58.wireOp",EDGE,"E190"),sQuery(id+"F58.wireOp",EDGE,"E191"),sQuery(id+"F58.wireOp",EDGE,"E192"),sQuery(id+"F58.wireOp",EDGE,"E193"),sQuery(id+"F58.wireOp",EDGE,"E194"),sQuery(id+"F58.wireOp",EDGE,"E195"),sQuery(id+"F58.wireOp",EDGE,"E196"),sQuery(id+"F58.wireOp",EDGE,"E199"),sQuery(id+"F58.wireOp",EDGE,"E200")])]});
            hole(context, id + "F61", {"style" : HoleStyle.SIMPLE, "endStyle" : HoleEndStyle.BLIND, "standardTappedOrClearance" : lookupTablePath({ "standard" : "ISO", "size" : "12", "type" : "Drilled" }), "standardBlindInLast" : lookupTablePath({ "standard" : "ISO", "size" : "12", "type" : "Drilled" }), "holeDiameter" : 12 * mm, "holeDepth" : 30 * mm, "locations" : qUnion([Q0, Q1]), "scope" : qUnion([Q2])});
        }
        {
            var Q0;
            Q0=makeQuery(id+"F59.opExtrude","SWEPT_BODY",BODY,{"disambiguationData":[OSD([sQuery(id+"F58.wireOp",EDGE,"E190"),sQuery(id+"F58.wireOp",EDGE,"E191"),sQuery(id+"F58.wireOp",EDGE,"E192"),sQuery(id+"F58.wireOp",EDGE,"E193"),sQuery(id+"F58.wireOp",EDGE,"E194"),sQuery(id+"F58.wireOp",EDGE,"E195"),sQuery(id+"F58.wireOp",EDGE,"E196"),sQuery(id+"F58.wireOp",EDGE,"E199"),sQuery(id+"F58.wireOp",EDGE,"E200")])]});
            var Q1;
            Q1=qCreatedBy(makeId("Right.planeOp"),FACE);
            mirror(context, id + "F62", {"entities" : qUnion([Q0]), "mirrorPlane" : qUnion([Q1])});
        }
        {
            var Q0;
            Q0=makeQuery(id+"F59.opExtrude","SWEPT_BODY",BODY,{"disambiguationData":[OSD([sQuery(id+"F58.wireOp",EDGE,"E190"),sQuery(id+"F58.wireOp",EDGE,"E191"),sQuery(id+"F58.wireOp",EDGE,"E192"),sQuery(id+"F58.wireOp",EDGE,"E193"),sQuery(id+"F58.wireOp",EDGE,"E194"),sQuery(id+"F58.wireOp",EDGE,"E195"),sQuery(id+"F58.wireOp",EDGE,"E196"),sQuery(id+"F58.wireOp",EDGE,"E199"),sQuery(id+"F58.wireOp",EDGE,"E200")])]});
            var Q1;
            Q1=qCreatedBy(id+"F55.planeOp",FACE);
            mirror(context, id + "F63", {"entities" : qUnion([Q0]), "mirrorPlane" : qUnion([Q1])});
        }
        {
            var Q0;
            Q0=makeQuery(id+"F63.opPattern","COPY",BODY,{"derivedFrom":makeQuery(id+"F59.opExtrude","SWEPT_BODY",BODY,{"disambiguationData":[OSD([sQuery(id+"F58.wireOp",EDGE,"E190"),sQuery(id+"F58.wireOp",EDGE,"E191"),sQuery(id+"F58.wireOp",EDGE,"E192"),sQuery(id+"F58.wireOp",EDGE,"E193"),sQuery(id+"F58.wireOp",EDGE,"E194"),sQuery(id+"F58.wireOp",EDGE,"E195"),sQuery(id+"F58.wireOp",EDGE,"E196"),sQuery(id+"F58.wireOp",EDGE,"E199"),sQuery(id+"F58.wireOp",EDGE,"E200")])]}),"instanceName":"1"});
            var Q1;
            Q1=qCreatedBy(makeId("Right.planeOp"),FACE);
            mirror(context, id + "F64", {"operationType" : NewBodyOperationType.ADD, "entities" : qUnion([Q0]), "mirrorPlane" : qUnion([Q1])});
        }
        {
            var Q0;
            Q0=makeQuery(id+"F5.opExtrude","SWEPT_EDGE",EDGE,{"disambiguationData":[OSD([sQuery(id+"F4.wireOp",EDGE,"E50.bottom"),sQuery(id+"F4.wireOp",EDGE,"E50.right")])]});
            var Q1;
            Q1=makeQuery(id+"F5.opExtrude","SWEPT_EDGE",EDGE,{"disambiguationData":[OSD([sQuery(id+"F4.wireOp",EDGE,"E50.top"),sQuery(id+"F4.wireOp",EDGE,"E52.trimOffspring")])]});
            chamfer(context, id + "F65", {"entities" : qUnion([Q0, Q1]), "width" : 5 * mm, "tangentPropagation" : true});
        }
        {
            var Q0;
            Q0=makeQuery(id+"F29.opPattern","COPY",EDGE,{"derivedFrom":makeQuery(id+"F5.opExtrude","SWEPT_EDGE",EDGE,{"disambiguationData":[OSD([sQuery(id+"F4.wireOp",EDGE,"E50.bottom"),sQuery(id+"F4.wireOp",EDGE,"E50.right")])]}),"instanceName":"1"});
            var Q1;
            Q1=makeQuery(id+"F29.opPattern","COPY",EDGE,{"derivedFrom":makeQuery(id+"F5.opExtrude","SWEPT_EDGE",EDGE,{"disambiguationData":[OSD([sQuery(id+"F4.wireOp",EDGE,"E50.top"),sQuery(id+"F4.wireOp",EDGE,"E52.trimOffspring")])]}),"instanceName":"1"});
            chamfer(context, id + "F66", {"entities" : qUnion([Q0, Q1]), "width" : 5 * mm, "tangentPropagation" : true});
        }
        {
            var Q0;
            Q0=makeQuery(id+"F63.opPattern","COPY",FACE,{"derivedFrom":makeQuery(id+"F59.opExtrude","CAP_FACE",FACE,{"disambiguationData":[OSD([sQuery(id+"F58.wireOp",EDGE,"E190"),sQuery(id+"F58.wireOp",EDGE,"E191"),sQuery(id+"F58.wireOp",EDGE,"E192"),sQuery(id+"F58.wireOp",EDGE,"E193"),sQuery(id+"F58.wireOp",EDGE,"E194"),sQuery(id+"F58.wireOp",EDGE,"E195"),sQuery(id+"F58.wireOp",EDGE,"E196"),sQuery(id+"F58.wireOp",EDGE,"E199"),sQuery(id+"F58.wireOp",EDGE,"E200")])],"isStart":false}),"instanceName":"1"});
            var sketch = newSketch(context, id + "F67", { "sketchPlane" : qUnion([Q0])});
            skLineSegment(sketch, "E208.0", {"start": v(-35, -113.53) * mm, "end": v(-35, -148.53) * mm, "construction": true});
            skLineSegment(sketch, "E209", {"start": v(-35, -131.03) * mm, "end": v(-367.6, -131.03) * mm, "construction": true});
            skLineSegment(sketch, "E210.0", {"start": v(-35, -16.03) * mm, "end": v(-367.6, -16.03) * mm, "construction": true});
            skLineSegment(sketch, "E211.0", {"start": v(-35, 23.97) * mm, "end": v(-367.6, 23.97) * mm, "construction": true});
            skLineSegment(sketch, "E212", {"start": v(0, 332.63) * mm, "end": v(0, -263.23) * mm, "construction": true});
            skLineSegment(sketch, "E213.0", {"start": v(-140, 23.97) * mm, "end": v(-140, -16.03) * mm, "construction": true});
            skLineSegment(sketch, "E214.trimOffspring", {"start": v(-140, -131.03) * mm, "end": v(-140, -263.23) * mm, "construction": true});
            skLineSegment(sketch, "E215.bottom", {"start": v(-160, 23.97) * mm, "end": v(-120, 23.97) * mm});
            skLineSegment(sketch, "E215.top", {"start": v(-160, -16.03) * mm, "end": v(-120, -16.03) * mm});
            skLineSegment(sketch, "E215.left", {"start": v(-160, 23.97) * mm, "end": v(-160, -16.03) * mm});
            skLineSegment(sketch, "E215.right", {"start": v(-120, 23.97) * mm, "end": v(-120, -16.03) * mm});
            skPoint(sketch, "E215.middle", {"position": v(-140, 3.97) * mm});
            skSolve(sketch);
        }
        {
            var Q0;
            Q0=qSketchRegion(id+"F67",true);
            extrude(context, id + "F68", {"entities" : qUnion([Q0]), "depth" : 60 * mm});
        }
        {
            var Q0;
            Q0=makeQuery(id+"F68.opExtrude","SWEPT_FACE",FACE,{"disambiguationData":[OSD([sQuery(id+"F67.wireOp",EDGE,"E215.bottom")])]});
            var sketch = newSketch(context, id + "F69", { "sketchPlane" : qUnion([Q0])});
            skLineSegment(sketch, "E216.0", {"start": v(917.5, -35) * mm, "end": v(952.5, -35) * mm, "construction": true});
            skLineSegment(sketch, "E217", {"start": v(935, -120) * mm, "end": v(935, -160) * mm, "construction": true});
            skLineSegment(sketch, "E218.0.0", {"start": v(896, -120) * mm, "end": v(896, -160) * mm, "construction": true});
            skLineSegment(sketch, "E218.0.1", {"start": v(896, -160) * mm, "end": v(956, -160) * mm, "construction": true});
            skLineSegment(sketch, "E218.0.2", {"start": v(956, -160) * mm, "end": v(956, -120) * mm, "construction": true});
            skLineSegment(sketch, "E218.0.3", {"start": v(956, -120) * mm, "end": v(896, -120) * mm, "construction": true});
            skLineSegment(sketch, "E219", {"start": v(956, -140) * mm, "end": v(857.2, -140) * mm, "construction": true});
            skPoint(sketch, "E219.endSnap0", {"position": v(956, -140) * mm});
            skPoint(sketch, "E220.orphan", {"position": v(935, -35) * mm});
            skPoint(sketch, "E221", {"position": v(935, -140) * mm});
            skSolve(sketch);
        }
        {
            var Q0;
            Q0=sQuery(id+"F69.wireOp",VERTEX,"E221");
            var Q1;
            Q1=makeQuery(id+"F68.opExtrude","SWEPT_BODY",BODY,{"disambiguationData":[OSD([sQuery(id+"F67.wireOp",EDGE,"E215.bottom"),sQuery(id+"F67.wireOp",EDGE,"E215.top"),sQuery(id+"F67.wireOp",EDGE,"E215.left"),sQuery(id+"F67.wireOp",EDGE,"E215.right")])]});
            hole(context, id + "F70", {"style" : HoleStyle.SIMPLE, "endStyle" : HoleEndStyle.THROUGH, "standardTappedOrClearance" : lookupTablePath({ "standard" : "ISO", "size" : "20", "type" : "Drilled" }), "standardBlindInLast" : lookupTablePath({ "standard" : "ISO", "size" : "20", "type" : "Drilled" }), "holeDiameter" : 20 * mm, "locations" : qUnion([Q0]), "scope" : qUnion([Q1]), "isTappedThrough" : true});
        }
        {
            var Q0;
            Q0=makeQuery(id+"F68.opExtrude","SWEPT_FACE",FACE,{"disambiguationData":[OSD([sQuery(id+"F67.wireOp",EDGE,"E215.left")])]});
            var sketch = newSketch(context, id + "F71", { "sketchPlane" : qUnion([Q0])});
            skLineSegment(sketch, "E222.0", {"start": v(925, 23.97) * mm, "end": v(945, 23.97) * mm, "construction": true});
            skLineSegment(sketch, "E223", {"start": v(935, 23.97) * mm, "end": v(935, -16.03) * mm, "construction": true});
            skLineSegment(sketch, "E224.0", {"start": v(956, -16.03) * mm, "end": v(896, -16.03) * mm, "construction": true});
            skPoint(sketch, "E225", {"position": v(935, 3.97) * mm});
            skSolve(sketch);
        }
        {
            var Q0;
            Q0=sQuery(id+"F71.wireOp",VERTEX,"E225");
            var Q1;
            Q1=makeQuery(id+"F68.opExtrude","SWEPT_BODY",BODY,{"disambiguationData":[OSD([sQuery(id+"F67.wireOp",EDGE,"E215.bottom"),sQuery(id+"F67.wireOp",EDGE,"E215.top"),sQuery(id+"F67.wireOp",EDGE,"E215.left"),sQuery(id+"F67.wireOp",EDGE,"E215.right")])]});
            hole(context, id + "F72", {"style" : HoleStyle.SIMPLE, "endStyle" : HoleEndStyle.THROUGH, "standardTappedOrClearance" : lookupTablePath({ "standard" : "ISO", "size" : "8", "type" : "Drilled" }), "standardBlindInLast" : lookupTablePath({ "standard" : "ISO", "size" : "8", "type" : "Drilled" }), "holeDiameter" : 8 * mm, "locations" : qUnion([Q0]), "scope" : qUnion([Q1]), "isTappedThrough" : true});
        }
        {
            var Q0;
            Q0=makeQuery(id+"F68.opExtrude","SWEPT_BODY",BODY,{"disambiguationData":[OSD([sQuery(id+"F67.wireOp",EDGE,"E215.bottom"),sQuery(id+"F67.wireOp",EDGE,"E215.top"),sQuery(id+"F67.wireOp",EDGE,"E215.left"),sQuery(id+"F67.wireOp",EDGE,"E215.right")])]});
            var Q1;
            Q1=qCreatedBy(makeId("Right.planeOp"),FACE);
            mirror(context, id + "F73", {"entities" : qUnion([Q0]), "mirrorPlane" : qUnion([Q1])});
        }
        {
            var Q0;
            Q0=makeQuery(id+"F51.opExtrude","SWEPT_BODY",BODY,{"disambiguationData":[OSD([sQuery(id+"F50.wireOp",EDGE,"E175.0.0"),sQuery(id+"F50.wireOp",EDGE,"E175.0.1"),sQuery(id+"F50.wireOp",EDGE,"E175.0.8"),sQuery(id+"F50.wireOp",EDGE,"E176")])]});
            var Q1;
            Q1=qCreatedBy(id+"F55.planeOp",FACE);
            mirror(context, id + "F74", {"entities" : qUnion([Q0]), "mirrorPlane" : qUnion([Q1])});
        }
        {
            var Q0;
            Q0=makeQuery(id+"F51.opExtrude","SWEPT_BODY",BODY,{"disambiguationData":[OSD([sQuery(id+"F50.wireOp",EDGE,"E175.0.0"),sQuery(id+"F50.wireOp",EDGE,"E175.0.1"),sQuery(id+"F50.wireOp",EDGE,"E175.0.8"),sQuery(id+"F50.wireOp",EDGE,"E176")])]});
            var Q1;
            Q1=makeQuery(id+"F74.opPattern","COPY",BODY,{"derivedFrom":makeQuery(id+"F51.opExtrude","SWEPT_BODY",BODY,{"disambiguationData":[OSD([sQuery(id+"F50.wireOp",EDGE,"E175.0.0"),sQuery(id+"F50.wireOp",EDGE,"E175.0.1"),sQuery(id+"F50.wireOp",EDGE,"E175.0.8"),sQuery(id+"F50.wireOp",EDGE,"E176")])]}),"instanceName":"1"});
            var Q2;
            Q2=qCreatedBy(makeId("Right.planeOp"),FACE);
            mirror(context, id + "F75", {"entities" : qUnion([Q0, Q1]), "mirrorPlane" : qUnion([Q2])});
        }
        {
            var Q0;
            Q0=makeQuery(id+"F1.opExtrude","SWEPT_BODY",BODY,{"disambiguationData":[OSD([sQuery(id+"F0.wireOp",EDGE,"E0.bottom"),sQuery(id+"F0.wireOp",EDGE,"E0.top"),sQuery(id+"F0.wireOp",EDGE,"E0.left"),sQuery(id+"F0.wireOp",EDGE,"E0.right"),sQuery(id+"F0.wireOp",EDGE,"E2.0"),sQuery(id+"F0.wireOp",EDGE,"E3.0"),sQuery(id+"F0.wireOp",EDGE,"E4.0"),sQuery(id+"F0.wireOp",EDGE,"E5.0"),sQuery(id+"F0.wireOp",EDGE,"E6.trimOffspring"),sQuery(id+"F0.wireOp",EDGE,"E7.trimOffspring"),sQuery(id+"F0.wireOp",EDGE,"E8.trimOffspring"),sQuery(id+"F0.wireOp",EDGE,"E9.trimOffspring"),sQuery(id+"F0.wireOp",EDGE,"E10.filletArc"),sQuery(id+"F0.wireOp",EDGE,"E11.filletArc"),sQuery(id+"F0.wireOp",EDGE,"E12.filletArc"),sQuery(id+"F0.wireOp",EDGE,"E13.filletArc")])]});
            var Q1;
            Q1=makeQuery(id+"F62.opPattern","COPY",BODY,{"derivedFrom":makeQuery(id+"F59.opExtrude","SWEPT_BODY",BODY,{"disambiguationData":[OSD([sQuery(id+"F58.wireOp",EDGE,"E190"),sQuery(id+"F58.wireOp",EDGE,"E191"),sQuery(id+"F58.wireOp",EDGE,"E192"),sQuery(id+"F58.wireOp",EDGE,"E193"),sQuery(id+"F58.wireOp",EDGE,"E194"),sQuery(id+"F58.wireOp",EDGE,"E195"),sQuery(id+"F58.wireOp",EDGE,"E196"),sQuery(id+"F58.wireOp",EDGE,"E199"),sQuery(id+"F58.wireOp",EDGE,"E200")])]}),"instanceName":"1"});
            var Q2;
            Q2=makeQuery(id+"F59.opExtrude","SWEPT_BODY",BODY,{"disambiguationData":[OSD([sQuery(id+"F58.wireOp",EDGE,"E190"),sQuery(id+"F58.wireOp",EDGE,"E191"),sQuery(id+"F58.wireOp",EDGE,"E192"),sQuery(id+"F58.wireOp",EDGE,"E193"),sQuery(id+"F58.wireOp",EDGE,"E194"),sQuery(id+"F58.wireOp",EDGE,"E195"),sQuery(id+"F58.wireOp",EDGE,"E196"),sQuery(id+"F58.wireOp",EDGE,"E199"),sQuery(id+"F58.wireOp",EDGE,"E200")])]});
            booleanBodies(context, id + "F76", {"operationType" : BooleanOperationType.UNION, "tools" : qUnion([Q0, Q1, Q2])});
        }
        {
            var Q0;
            Q0=makeQuery(id+"F1.opExtrude","SWEPT_FACE",FACE,{"disambiguationData":[OSD([sQuery(id+"F0.wireOp",EDGE,"E8.trimOffspring")])]});
            var sketch = newSketch(context, id + "F77", { "sketchPlane" : qUnion([Q0])});
            skLineSegment(sketch, "E226.0", {"start": v(990, -81.03) * mm, "end": v(-990, -81.03) * mm, "construction": true});
            skLineSegment(sketch, "E227", {"start": v(0, 255.13) * mm, "end": v(0, -180.02) * mm, "construction": true});
            skLineSegment(sketch, "E228.0", {"start": v(990, 18.97) * mm, "end": v(-990, 18.97) * mm, "construction": true});
            skLineSegment(sketch, "E229.0", {"start": v(1002.25, -56.03) * mm, "end": v(-990, -56.03) * mm, "construction": true});
            skArc(sketch, "E230", {"start": v(81.12, -56.03) * mm, "mid": v(6.12, 18.97) * mm, "end": v(-68.88, -56.03) * mm});
            skLineSegment(sketch, "E231", {"start": v(-68.88, -56.03) * mm, "end": v(-68.87, -81.03) * mm});
            skLineSegment(sketch, "E232", {"start": v(81.12, -56.03) * mm, "end": v(81.12, -81.03) * mm});
            skLineSegment(sketch, "E233.0", {"start": v(-80, -56.03) * mm, "end": v(-80, -81.03) * mm});
            skArc(sketch, "E233.1", {"start": v(92.25, -56.03) * mm, "mid": v(6.13, 30.1) * mm, "end": v(-80, -56.03) * mm});
            skLineSegment(sketch, "E233.2", {"start": v(92.25, -56.03) * mm, "end": v(92.25, -81.03) * mm});
            skLineSegment(sketch, "E234", {"start": v(-80, -81.03) * mm, "end": v(-68.87, -81.03) * mm});
            skLineSegment(sketch, "E235", {"start": v(81.12, -81.03) * mm, "end": v(92.25, -81.03) * mm});
            skSolve(sketch);
        }
        {
            var Q0;
            Q0 = qSketchRegion(id + "F77", true);
            var Q1;
            Q1=makeQuery(id+"F1.opExtrude","SWEPT_FACE",FACE,{"disambiguationData":[OSD([sQuery(id+"F0.wireOp",EDGE,"E9.trimOffspring")])]});
            extrude(context, id + "F78", {"entities" : qUnion([Q0]), "operationType" : NewBodyOperationType.ADD, "endBound" : BoundingType.UP_TO_SURFACE, "oppositeDirection" : true, "endBoundEntityFace" : qUnion([Q1]), "depth" : 25 * mm});
        }
        {
            var Q0;
            Q0=makeQuery(id+"F78.boolean.opBoolean","MERGE",FACE,{"derivedFrom":[makeQuery(id+"F1.opExtrude","SWEPT_FACE",FACE,{"disambiguationData":[OSD([sQuery(id+"F0.wireOp",EDGE,"E8.trimOffspring")])]}),makeQuery(id+"F78.opExtrude","CAP_FACE",FACE,{"disambiguationData":[OSD([sQuery(id+"F77.wireOp",EDGE,"E230"),sQuery(id+"F77.wireOp",EDGE,"E231"),sQuery(id+"F77.wireOp",EDGE,"E232"),sQuery(id+"F77.wireOp",EDGE,"E233.0"),sQuery(id+"F77.wireOp",EDGE,"E233.1"),sQuery(id+"F77.wireOp",EDGE,"E233.2"),sQuery(id+"F77.wireOp",EDGE,"E234"),sQuery(id+"F77.wireOp",EDGE,"E235")])],"isStart":true})]});
            var sketch = newSketch(context, id + "F79", { "sketchPlane" : qUnion([Q0])});
            skArc(sketch, "E236.0", {"start": v(81.12, -56.03) * mm, "mid": v(6.12, 18.97) * mm, "end": v(-68.88, -56.03) * mm});
            skLineSegment(sketch, "E237.0", {"start": v(-68.88, -56.03) * mm, "end": v(-68.87, -81.03) * mm});
            skLineSegment(sketch, "E238.0", {"start": v(81.12, -56.03) * mm, "end": v(81.12, -81.03) * mm});
            skLineSegment(sketch, "E239.0", {"start": v(81.12, -81.03) * mm, "end": v(-68.88, -81.03) * mm});
            skPoint(sketch, "E240.orphan", {"position": v(81.12, -69.47) * mm});
            skPoint(sketch, "E241.orphan", {"position": v(-68.87, -69.47) * mm});
            skPoint(sketch, "E242.orphan", {"position": v(990, -81.03) * mm});
            skPoint(sketch, "E243.orphan", {"position": v(-990, -81.03) * mm});
            skSolve(sketch);
        }
        {
            var Q0;
            Q0 = qSketchRegion(id + "F79", true);
            var Q1;
            {var subQ0=sQuery(id+"F0.wireOp",EDGE,"E9.trimOffspring");Q1=makeQuery(id+"F78.boolean.opBoolean","MERGE",FACE,{"derivedFrom":[makeQuery(id+"F1.opExtrude","SWEPT_FACE",FACE,{"disambiguationData":[OSD([subQ0])]}),makeQuery(id+"F78.opExtrude","CAP_FACE",FACE,{"disambiguationData":[OSD([subQ0])],"isStart":false})]});}
            extrude(context, id + "F80", {"entities" : qUnion([Q0]), "operationType" : NewBodyOperationType.REMOVE, "endBound" : BoundingType.UP_TO_SURFACE, "oppositeDirection" : true, "endBoundEntityFace" : qUnion([Q1]), "depth" : 25 * mm});
        }
    });
